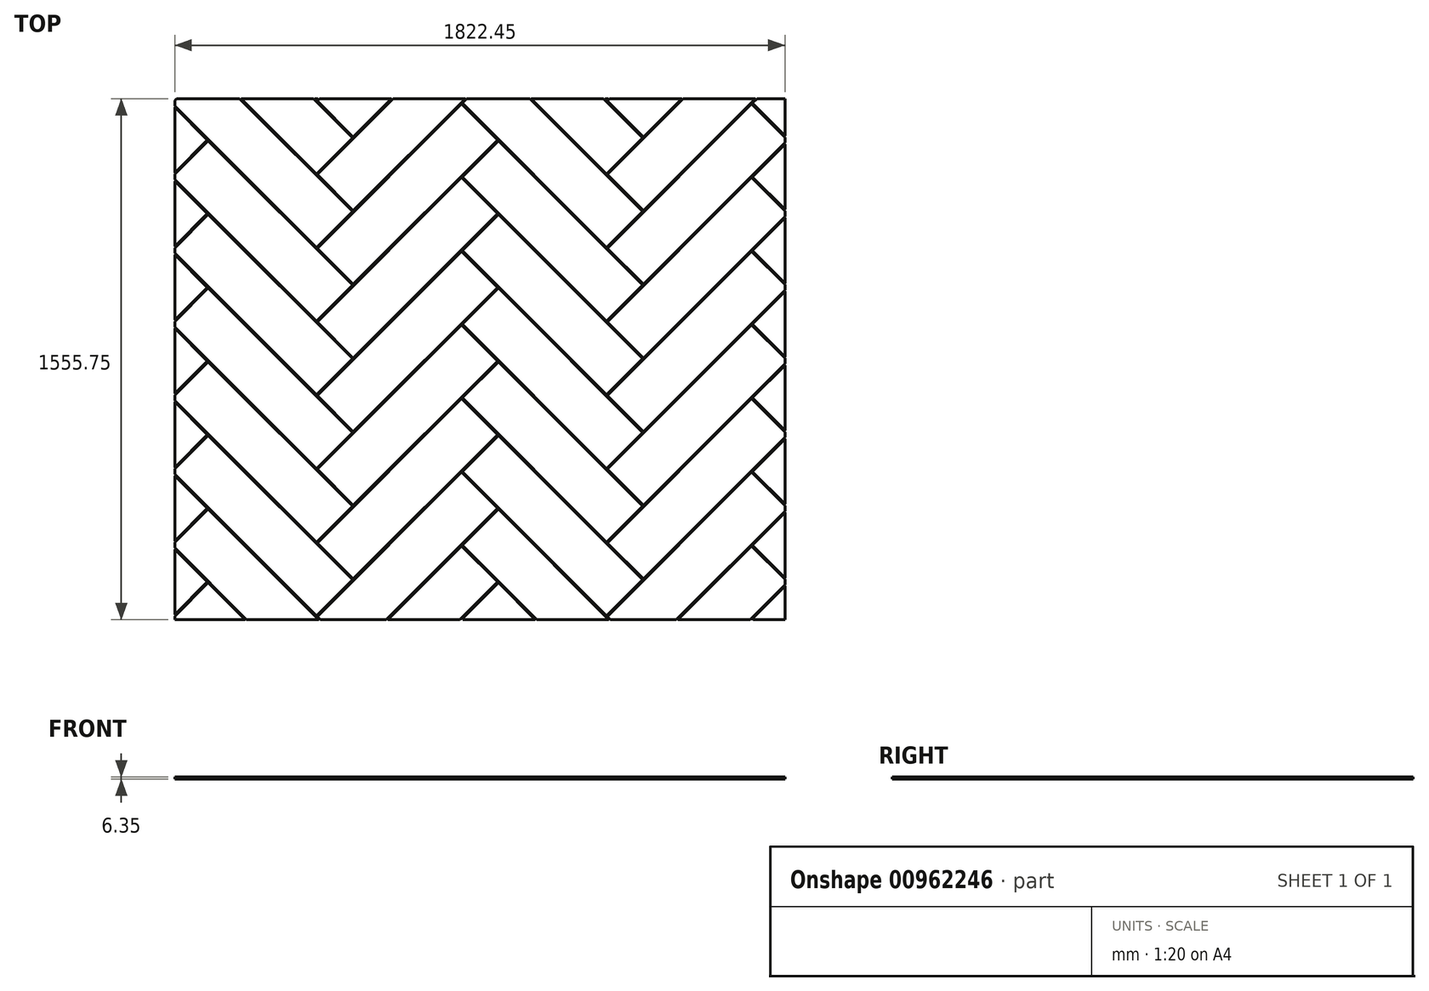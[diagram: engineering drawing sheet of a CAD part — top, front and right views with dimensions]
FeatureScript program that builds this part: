
annotation { "Feature Type Name" : "Feature", "Feature Type Description" : "" }
export const myFeature = defineFeature(function(context is Context, id is Id, definition is map)
    precondition{}
    {
        {
            var Q0;
            Q0=qCreatedBy(makeId("Top.planeOp"),FACE);
            var sketch = newSketch(context, id + "F0", { "sketchPlane" : qUnion([Q0])});
            skLineSegment(sketch, "E0.bottom", {"start": v(0, 0) * mm, "end": v(609.6, 0) * mm});
            skLineSegment(sketch, "E0.top", {"start": v(0, 152.4) * mm, "end": v(609.6, 152.4) * mm});
            skLineSegment(sketch, "E0.left", {"start": v(0, 0) * mm, "end": v(0, 152.4) * mm});
            skLineSegment(sketch, "E0.right", {"start": v(609.6, 0) * mm, "end": v(609.6, 152.4) * mm});
            skLineSegment(sketch, "E1.bottom", {"start": v(152.4, 155.57) * mm, "end": v(152.4, 765.17) * mm});
            skLineSegment(sketch, "E1.top", {"start": v(0, 155.58) * mm, "end": v(0, 765.17) * mm});
            skLineSegment(sketch, "E1.left", {"start": v(152.4, 155.57) * mm, "end": v(0, 155.57) * mm});
            skLineSegment(sketch, "E1.right", {"start": v(152.4, 765.17) * mm, "end": v(0, 765.17) * mm});
            skLineSegment(sketch, "E2.bottom", {"start": v(155.58, 155.57) * mm, "end": v(765.17, 155.57) * mm});
            skLineSegment(sketch, "E2.top", {"start": v(155.58, 307.98) * mm, "end": v(765.17, 307.97) * mm});
            skLineSegment(sketch, "E2.left", {"start": v(155.58, 155.58) * mm, "end": v(155.58, 307.98) * mm});
            skLineSegment(sketch, "E2.right", {"start": v(765.17, 155.57) * mm, "end": v(765.17, 307.97) * mm});
            skLineSegment(sketch, "E3.bottom", {"start": v(307.98, 311.15) * mm, "end": v(307.98, 920.75) * mm});
            skLineSegment(sketch, "E3.top", {"start": v(155.58, 311.15) * mm, "end": v(155.58, 920.75) * mm});
            skLineSegment(sketch, "E3.left", {"start": v(307.98, 311.15) * mm, "end": v(155.58, 311.15) * mm});
            skLineSegment(sketch, "E3.right", {"start": v(307.98, 920.75) * mm, "end": v(155.58, 920.75) * mm});
            skLineSegment(sketch, "E4.0.1.0", {"start": v(-612.78, 612.78) * mm, "end": v(-3.18, 612.78) * mm});
            skLineSegment(sketch, "E4.0.1.1", {"start": v(-460.37, 768.35) * mm, "end": v(-612.77, 768.35) * mm});
            skLineSegment(sketch, "E4.0.1.2", {"start": v(-457.2, 768.35) * mm, "end": v(-457.2, 920.75) * mm});
            skLineSegment(sketch, "E4.0.1.3", {"start": v(-304.8, 923.92) * mm, "end": v(-457.2, 923.92) * mm});
            skLineSegment(sketch, "E4.0.1.4", {"start": v(-457.2, 768.35) * mm, "end": v(152.4, 768.35) * mm});
            skLineSegment(sketch, "E4.0.1.5", {"start": v(-460.37, 768.35) * mm, "end": v(-460.37, 1377.95) * mm});
            skLineSegment(sketch, "E4.0.1.6", {"start": v(-457.2, 920.75) * mm, "end": v(152.4, 920.75) * mm});
            skLineSegment(sketch, "E4.0.1.7", {"start": v(-304.8, 1533.52) * mm, "end": v(-457.2, 1533.52) * mm});
            skLineSegment(sketch, "E4.0.1.8", {"start": v(-612.78, 768.35) * mm, "end": v(-612.77, 1377.95) * mm});
            skLineSegment(sketch, "E4.0.1.9", {"start": v(-457.2, 923.92) * mm, "end": v(-457.2, 1533.52) * mm});
            skLineSegment(sketch, "E4.0.1.10", {"start": v(-3.18, 612.78) * mm, "end": v(-3.18, 765.17) * mm});
            skLineSegment(sketch, "E4.0.1.11", {"start": v(-304.8, 923.92) * mm, "end": v(-304.8, 1533.52) * mm});
            skLineSegment(sketch, "E4.0.1.12", {"start": v(-612.78, 612.78) * mm, "end": v(-612.78, 765.17) * mm});
            skLineSegment(sketch, "E4.0.1.13", {"start": v(-460.37, 1377.95) * mm, "end": v(-612.77, 1377.95) * mm});
            skLineSegment(sketch, "E4.0.1.14", {"start": v(152.4, 768.35) * mm, "end": v(152.4, 920.75) * mm});
            skLineSegment(sketch, "E4.0.1.15", {"start": v(-612.77, 765.17) * mm, "end": v(-3.17, 765.17) * mm});
            skLineSegment(sketch, "E4.1.0.0", {"start": v(311.15, 311.15) * mm, "end": v(920.75, 311.15) * mm});
            skLineSegment(sketch, "E4.1.0.1", {"start": v(463.55, 466.72) * mm, "end": v(311.15, 466.72) * mm});
            skLineSegment(sketch, "E4.1.0.2", {"start": v(466.73, 466.72) * mm, "end": v(466.73, 619.12) * mm});
            skLineSegment(sketch, "E4.1.0.3", {"start": v(619.13, 622.3) * mm, "end": v(466.73, 622.3) * mm});
            skLineSegment(sketch, "E4.1.0.4", {"start": v(466.73, 466.72) * mm, "end": v(1076.33, 466.72) * mm});
            skLineSegment(sketch, "E4.1.0.5", {"start": v(463.55, 466.72) * mm, "end": v(463.55, 1076.32) * mm});
            skLineSegment(sketch, "E4.1.0.6", {"start": v(466.73, 619.12) * mm, "end": v(1076.33, 619.12) * mm});
            skLineSegment(sketch, "E4.1.0.7", {"start": v(619.13, 1231.9) * mm, "end": v(466.73, 1231.9) * mm});
            skLineSegment(sketch, "E4.1.0.8", {"start": v(311.15, 466.72) * mm, "end": v(311.15, 1076.32) * mm});
            skLineSegment(sketch, "E4.1.0.9", {"start": v(466.73, 622.3) * mm, "end": v(466.73, 1231.9) * mm});
            skLineSegment(sketch, "E4.1.0.10", {"start": v(920.75, 311.15) * mm, "end": v(920.75, 463.55) * mm});
            skLineSegment(sketch, "E4.1.0.11", {"start": v(619.13, 622.3) * mm, "end": v(619.13, 1231.9) * mm});
            skLineSegment(sketch, "E4.1.0.12", {"start": v(311.15, 311.15) * mm, "end": v(311.15, 463.55) * mm});
            skLineSegment(sketch, "E4.1.0.13", {"start": v(463.55, 1076.32) * mm, "end": v(311.15, 1076.32) * mm});
            skLineSegment(sketch, "E4.1.0.14", {"start": v(1076.32, 466.72) * mm, "end": v(1076.32, 619.12) * mm});
            skLineSegment(sketch, "E4.1.0.15", {"start": v(311.15, 463.55) * mm, "end": v(920.75, 463.55) * mm});
            skLineSegment(sketch, "E4.1.1.0", {"start": v(-301.62, 923.92) * mm, "end": v(307.98, 923.92) * mm});
            skLineSegment(sketch, "E4.1.1.1", {"start": v(-149.22, 1079.5) * mm, "end": v(-301.62, 1079.5) * mm});
            skLineSegment(sketch, "E4.1.1.2", {"start": v(-146.05, 1079.5) * mm, "end": v(-146.05, 1231.9) * mm});
            skLineSegment(sketch, "E4.1.1.3", {"start": v(6.35, 1235.07) * mm, "end": v(-146.05, 1235.07) * mm});
            skLineSegment(sketch, "E4.1.1.4", {"start": v(-146.05, 1079.5) * mm, "end": v(463.55, 1079.5) * mm});
            skLineSegment(sketch, "E4.1.1.5", {"start": v(-149.22, 1079.5) * mm, "end": v(-149.22, 1689.1) * mm});
            skLineSegment(sketch, "E4.1.1.6", {"start": v(-146.05, 1231.9) * mm, "end": v(463.55, 1231.9) * mm});
            skLineSegment(sketch, "E4.1.1.7", {"start": v(6.35, 1844.67) * mm, "end": v(-146.05, 1844.67) * mm});
            skLineSegment(sketch, "E4.1.1.8", {"start": v(-301.62, 1079.5) * mm, "end": v(-301.62, 1689.1) * mm});
            skLineSegment(sketch, "E4.1.1.9", {"start": v(-146.05, 1235.07) * mm, "end": v(-146.05, 1844.67) * mm});
            skLineSegment(sketch, "E4.1.1.10", {"start": v(307.98, 923.92) * mm, "end": v(307.98, 1076.32) * mm});
            skLineSegment(sketch, "E4.1.1.11", {"start": v(6.35, 1235.07) * mm, "end": v(6.35, 1844.67) * mm});
            skLineSegment(sketch, "E4.1.1.12", {"start": v(-301.62, 923.92) * mm, "end": v(-301.62, 1076.32) * mm});
            skLineSegment(sketch, "E4.1.1.13", {"start": v(-149.22, 1689.1) * mm, "end": v(-301.62, 1689.1) * mm});
            skLineSegment(sketch, "E4.1.1.14", {"start": v(463.55, 1079.5) * mm, "end": v(463.55, 1231.9) * mm});
            skLineSegment(sketch, "E4.1.1.15", {"start": v(-301.62, 1076.32) * mm, "end": v(307.98, 1076.32) * mm});
            skLineSegment(sketch, "E4.2.0.0", {"start": v(622.3, 622.3) * mm, "end": v(1231.9, 622.3) * mm});
            skLineSegment(sketch, "E4.2.0.1", {"start": v(774.7, 777.87) * mm, "end": v(622.3, 777.87) * mm});
            skLineSegment(sketch, "E4.2.0.2", {"start": v(777.88, 777.87) * mm, "end": v(777.88, 930.27) * mm});
            skLineSegment(sketch, "E4.2.0.3", {"start": v(930.28, 933.45) * mm, "end": v(777.88, 933.45) * mm});
            skLineSegment(sketch, "E4.2.0.4", {"start": v(777.88, 777.87) * mm, "end": v(1387.47, 777.87) * mm});
            skLineSegment(sketch, "E4.2.0.5", {"start": v(774.7, 777.87) * mm, "end": v(774.7, 1387.47) * mm});
            skLineSegment(sketch, "E4.2.0.6", {"start": v(777.88, 930.27) * mm, "end": v(1387.47, 930.27) * mm});
            skLineSegment(sketch, "E4.2.0.7", {"start": v(930.28, 1543.05) * mm, "end": v(777.88, 1543.05) * mm});
            skLineSegment(sketch, "E4.2.0.8", {"start": v(622.3, 777.87) * mm, "end": v(622.3, 1387.47) * mm});
            skLineSegment(sketch, "E4.2.0.9", {"start": v(777.88, 933.45) * mm, "end": v(777.88, 1543.05) * mm});
            skLineSegment(sketch, "E4.2.0.10", {"start": v(1231.9, 622.3) * mm, "end": v(1231.9, 774.7) * mm});
            skLineSegment(sketch, "E4.2.0.11", {"start": v(930.28, 933.45) * mm, "end": v(930.28, 1543.05) * mm});
            skLineSegment(sketch, "E4.2.0.12", {"start": v(622.3, 622.3) * mm, "end": v(622.3, 774.7) * mm});
            skLineSegment(sketch, "E4.2.0.13", {"start": v(774.7, 1387.47) * mm, "end": v(622.3, 1387.47) * mm});
            skLineSegment(sketch, "E4.2.0.14", {"start": v(1387.47, 777.87) * mm, "end": v(1387.47, 930.27) * mm});
            skLineSegment(sketch, "E4.2.0.15", {"start": v(622.3, 774.7) * mm, "end": v(1231.9, 774.7) * mm});
            skLineSegment(sketch, "E4.2.1.0", {"start": v(9.53, 1235.07) * mm, "end": v(619.13, 1235.07) * mm});
            skLineSegment(sketch, "E4.2.1.1", {"start": v(161.93, 1390.65) * mm, "end": v(9.53, 1390.65) * mm});
            skLineSegment(sketch, "E4.2.1.2", {"start": v(165.1, 1390.65) * mm, "end": v(165.1, 1543.05) * mm});
            skLineSegment(sketch, "E4.2.1.3", {"start": v(317.5, 1546.22) * mm, "end": v(165.1, 1546.22) * mm});
            skLineSegment(sketch, "E4.2.1.4", {"start": v(165.1, 1390.65) * mm, "end": v(774.7, 1390.65) * mm});
            skLineSegment(sketch, "E4.2.1.5", {"start": v(161.93, 1390.65) * mm, "end": v(161.93, 2000.25) * mm});
            skLineSegment(sketch, "E4.2.1.6", {"start": v(165.1, 1543.05) * mm, "end": v(774.7, 1543.05) * mm});
            skLineSegment(sketch, "E4.2.1.7", {"start": v(317.5, 2155.82) * mm, "end": v(165.1, 2155.82) * mm});
            skLineSegment(sketch, "E4.2.1.8", {"start": v(9.53, 1390.65) * mm, "end": v(9.53, 2000.25) * mm});
            skLineSegment(sketch, "E4.2.1.9", {"start": v(165.1, 1546.22) * mm, "end": v(165.1, 2155.82) * mm});
            skLineSegment(sketch, "E4.2.1.10", {"start": v(619.13, 1235.07) * mm, "end": v(619.13, 1387.47) * mm});
            skLineSegment(sketch, "E4.2.1.11", {"start": v(317.5, 1546.22) * mm, "end": v(317.5, 2155.82) * mm});
            skLineSegment(sketch, "E4.2.1.12", {"start": v(9.53, 1235.07) * mm, "end": v(9.53, 1387.47) * mm});
            skLineSegment(sketch, "E4.2.1.13", {"start": v(161.93, 2000.25) * mm, "end": v(9.53, 2000.25) * mm});
            skLineSegment(sketch, "E4.2.1.14", {"start": v(774.7, 1390.65) * mm, "end": v(774.7, 1543.05) * mm});
            skLineSegment(sketch, "E4.2.1.15", {"start": v(9.53, 1387.47) * mm, "end": v(619.13, 1387.47) * mm});
            skLineSegment(sketch, "E4.direction1", {"start": v(0, 0) * mm, "end": v(311.15, 311.15) * mm, "construction": true});
            skLineSegment(sketch, "E4.direction2", {"start": v(0, 0) * mm, "end": v(-612.78, 612.78) * mm, "construction": true});
            skLineSegment(sketch, "E5.0.3.0", {"start": v(933.45, 933.45) * mm, "end": v(1543.05, 933.45) * mm});
            skLineSegment(sketch, "E5.3.3.0", {"start": v(1085.85, 1089.02) * mm, "end": v(933.45, 1089.02) * mm});
            skLineSegment(sketch, "E5.6.3.0", {"start": v(1089.03, 1089.02) * mm, "end": v(1089.03, 1241.42) * mm});
            skLineSegment(sketch, "E5.9.3.0", {"start": v(1241.43, 1244.6) * mm, "end": v(1089.03, 1244.6) * mm});
            skLineSegment(sketch, "E5.12.3.0", {"start": v(1089.03, 1089.02) * mm, "end": v(1698.62, 1089.02) * mm});
            skLineSegment(sketch, "E5.15.3.0", {"start": v(1085.85, 1089.02) * mm, "end": v(1085.85, 1698.62) * mm});
            skLineSegment(sketch, "E5.18.3.0", {"start": v(1089.03, 1241.42) * mm, "end": v(1698.62, 1241.42) * mm});
            skLineSegment(sketch, "E5.21.3.0", {"start": v(1241.43, 1854.2) * mm, "end": v(1089.03, 1854.2) * mm});
            skLineSegment(sketch, "E5.24.3.0", {"start": v(933.45, 1089.02) * mm, "end": v(933.45, 1698.62) * mm});
            skLineSegment(sketch, "E5.27.3.0", {"start": v(1089.03, 1244.6) * mm, "end": v(1089.03, 1854.2) * mm});
            skLineSegment(sketch, "E5.30.3.0", {"start": v(1543.05, 933.45) * mm, "end": v(1543.05, 1085.85) * mm});
            skLineSegment(sketch, "E5.33.3.0", {"start": v(1241.43, 1244.6) * mm, "end": v(1241.43, 1854.2) * mm});
            skLineSegment(sketch, "E5.36.3.0", {"start": v(933.45, 933.45) * mm, "end": v(933.45, 1085.85) * mm});
            skLineSegment(sketch, "E5.39.3.0", {"start": v(1085.85, 1698.62) * mm, "end": v(933.45, 1698.62) * mm});
            skLineSegment(sketch, "E5.42.3.0", {"start": v(1698.62, 1089.02) * mm, "end": v(1698.62, 1241.42) * mm});
            skLineSegment(sketch, "E5.45.3.0", {"start": v(933.45, 1085.85) * mm, "end": v(1543.05, 1085.85) * mm});
            skLineSegment(sketch, "E5.0.3.1", {"start": v(320.68, 1546.22) * mm, "end": v(930.28, 1546.22) * mm});
            skLineSegment(sketch, "E5.3.3.1", {"start": v(473.08, 1701.8) * mm, "end": v(320.68, 1701.8) * mm});
            skLineSegment(sketch, "E5.6.3.1", {"start": v(476.25, 1701.8) * mm, "end": v(476.25, 1854.2) * mm});
            skLineSegment(sketch, "E5.9.3.1", {"start": v(628.65, 1857.37) * mm, "end": v(476.25, 1857.37) * mm});
            skLineSegment(sketch, "E5.12.3.1", {"start": v(476.25, 1701.8) * mm, "end": v(1085.85, 1701.8) * mm});
            skLineSegment(sketch, "E5.15.3.1", {"start": v(473.08, 1701.8) * mm, "end": v(473.08, 2311.4) * mm});
            skLineSegment(sketch, "E5.18.3.1", {"start": v(476.25, 1854.2) * mm, "end": v(1085.85, 1854.2) * mm});
            skLineSegment(sketch, "E5.21.3.1", {"start": v(628.65, 2466.97) * mm, "end": v(476.25, 2466.97) * mm});
            skLineSegment(sketch, "E5.24.3.1", {"start": v(320.68, 1701.8) * mm, "end": v(320.68, 2311.4) * mm});
            skLineSegment(sketch, "E5.27.3.1", {"start": v(476.25, 1857.37) * mm, "end": v(476.25, 2466.97) * mm});
            skLineSegment(sketch, "E5.30.3.1", {"start": v(930.28, 1546.22) * mm, "end": v(930.28, 1698.62) * mm});
            skLineSegment(sketch, "E5.33.3.1", {"start": v(628.65, 1857.37) * mm, "end": v(628.65, 2466.97) * mm});
            skLineSegment(sketch, "E5.36.3.1", {"start": v(320.68, 1546.22) * mm, "end": v(320.68, 1698.62) * mm});
            skLineSegment(sketch, "E5.39.3.1", {"start": v(473.08, 2311.4) * mm, "end": v(320.68, 2311.4) * mm});
            skLineSegment(sketch, "E5.42.3.1", {"start": v(1085.85, 1701.8) * mm, "end": v(1085.85, 1854.2) * mm});
            skLineSegment(sketch, "E5.45.3.1", {"start": v(320.68, 1698.62) * mm, "end": v(930.28, 1698.62) * mm});
            skLineSegment(sketch, "E5.0.4.0", {"start": v(1244.6, 1244.6) * mm, "end": v(1854.2, 1244.6) * mm});
            skLineSegment(sketch, "E5.3.4.0", {"start": v(1397, 1400.17) * mm, "end": v(1244.6, 1400.17) * mm});
            skLineSegment(sketch, "E5.6.4.0", {"start": v(1400.18, 1400.17) * mm, "end": v(1400.18, 1552.57) * mm});
            skLineSegment(sketch, "E5.9.4.0", {"start": v(1552.58, 1555.75) * mm, "end": v(1400.18, 1555.75) * mm});
            skLineSegment(sketch, "E5.12.4.0", {"start": v(1400.18, 1400.17) * mm, "end": v(2009.78, 1400.17) * mm});
            skLineSegment(sketch, "E5.15.4.0", {"start": v(1397, 1400.17) * mm, "end": v(1397, 2009.77) * mm});
            skLineSegment(sketch, "E5.18.4.0", {"start": v(1400.18, 1552.57) * mm, "end": v(2009.78, 1552.57) * mm});
            skLineSegment(sketch, "E5.21.4.0", {"start": v(1552.58, 2165.35) * mm, "end": v(1400.18, 2165.35) * mm});
            skLineSegment(sketch, "E5.24.4.0", {"start": v(1244.6, 1400.17) * mm, "end": v(1244.6, 2009.77) * mm});
            skLineSegment(sketch, "E5.27.4.0", {"start": v(1400.18, 1555.75) * mm, "end": v(1400.18, 2165.35) * mm});
            skLineSegment(sketch, "E5.30.4.0", {"start": v(1854.2, 1244.6) * mm, "end": v(1854.2, 1397) * mm});
            skLineSegment(sketch, "E5.33.4.0", {"start": v(1552.58, 1555.75) * mm, "end": v(1552.58, 2165.35) * mm});
            skLineSegment(sketch, "E5.36.4.0", {"start": v(1244.6, 1244.6) * mm, "end": v(1244.6, 1397) * mm});
            skLineSegment(sketch, "E5.39.4.0", {"start": v(1397, 2009.77) * mm, "end": v(1244.6, 2009.77) * mm});
            skLineSegment(sketch, "E5.42.4.0", {"start": v(2009.78, 1400.17) * mm, "end": v(2009.78, 1552.57) * mm});
            skLineSegment(sketch, "E5.45.4.0", {"start": v(1244.6, 1397) * mm, "end": v(1854.2, 1397) * mm});
            skLineSegment(sketch, "E5.0.4.1", {"start": v(631.83, 1857.37) * mm, "end": v(1241.43, 1857.37) * mm});
            skLineSegment(sketch, "E5.3.4.1", {"start": v(784.23, 2012.95) * mm, "end": v(631.83, 2012.95) * mm});
            skLineSegment(sketch, "E5.6.4.1", {"start": v(787.4, 2012.95) * mm, "end": v(787.4, 2165.35) * mm});
            skLineSegment(sketch, "E5.9.4.1", {"start": v(939.8, 2168.52) * mm, "end": v(787.4, 2168.52) * mm});
            skLineSegment(sketch, "E5.12.4.1", {"start": v(787.4, 2012.95) * mm, "end": v(1397, 2012.95) * mm});
            skLineSegment(sketch, "E5.15.4.1", {"start": v(784.23, 2012.95) * mm, "end": v(784.23, 2622.55) * mm});
            skLineSegment(sketch, "E5.18.4.1", {"start": v(787.4, 2165.35) * mm, "end": v(1397, 2165.35) * mm});
            skLineSegment(sketch, "E5.21.4.1", {"start": v(939.8, 2778.12) * mm, "end": v(787.4, 2778.12) * mm});
            skLineSegment(sketch, "E5.24.4.1", {"start": v(631.83, 2012.95) * mm, "end": v(631.83, 2622.55) * mm});
            skLineSegment(sketch, "E5.27.4.1", {"start": v(787.4, 2168.52) * mm, "end": v(787.4, 2778.12) * mm});
            skLineSegment(sketch, "E5.30.4.1", {"start": v(1241.43, 1857.37) * mm, "end": v(1241.43, 2009.77) * mm});
            skLineSegment(sketch, "E5.33.4.1", {"start": v(939.8, 2168.52) * mm, "end": v(939.8, 2778.12) * mm});
            skLineSegment(sketch, "E5.36.4.1", {"start": v(631.83, 1857.37) * mm, "end": v(631.83, 2009.77) * mm});
            skLineSegment(sketch, "E5.39.4.1", {"start": v(784.23, 2622.55) * mm, "end": v(631.83, 2622.55) * mm});
            skLineSegment(sketch, "E5.42.4.1", {"start": v(1397, 2012.95) * mm, "end": v(1397, 2165.35) * mm});
            skLineSegment(sketch, "E5.45.4.1", {"start": v(631.83, 2009.77) * mm, "end": v(1241.43, 2009.77) * mm});
            skLineSegment(sketch, "E5.0.5.0", {"start": v(1555.75, 1555.75) * mm, "end": v(2165.35, 1555.75) * mm});
            skLineSegment(sketch, "E5.3.5.0", {"start": v(1708.15, 1711.32) * mm, "end": v(1555.75, 1711.32) * mm});
            skLineSegment(sketch, "E5.6.5.0", {"start": v(1711.33, 1711.32) * mm, "end": v(1711.33, 1863.72) * mm});
            skLineSegment(sketch, "E5.9.5.0", {"start": v(1863.73, 1866.9) * mm, "end": v(1711.33, 1866.9) * mm});
            skLineSegment(sketch, "E5.12.5.0", {"start": v(1711.33, 1711.32) * mm, "end": v(2320.92, 1711.32) * mm});
            skLineSegment(sketch, "E5.15.5.0", {"start": v(1708.15, 1711.32) * mm, "end": v(1708.15, 2320.92) * mm});
            skLineSegment(sketch, "E5.18.5.0", {"start": v(1711.33, 1863.72) * mm, "end": v(2320.92, 1863.72) * mm});
            skLineSegment(sketch, "E5.21.5.0", {"start": v(1863.73, 2476.5) * mm, "end": v(1711.33, 2476.5) * mm});
            skLineSegment(sketch, "E5.24.5.0", {"start": v(1555.75, 1711.32) * mm, "end": v(1555.75, 2320.92) * mm});
            skLineSegment(sketch, "E5.27.5.0", {"start": v(1711.33, 1866.9) * mm, "end": v(1711.33, 2476.5) * mm});
            skLineSegment(sketch, "E5.30.5.0", {"start": v(2165.35, 1555.75) * mm, "end": v(2165.35, 1708.15) * mm});
            skLineSegment(sketch, "E5.33.5.0", {"start": v(1863.73, 1866.9) * mm, "end": v(1863.73, 2476.5) * mm});
            skLineSegment(sketch, "E5.36.5.0", {"start": v(1555.75, 1555.75) * mm, "end": v(1555.75, 1708.15) * mm});
            skLineSegment(sketch, "E5.39.5.0", {"start": v(1708.15, 2320.92) * mm, "end": v(1555.75, 2320.92) * mm});
            skLineSegment(sketch, "E5.42.5.0", {"start": v(2320.92, 1711.32) * mm, "end": v(2320.92, 1863.72) * mm});
            skLineSegment(sketch, "E5.45.5.0", {"start": v(1555.75, 1708.15) * mm, "end": v(2165.35, 1708.15) * mm});
            skLineSegment(sketch, "E5.0.5.1", {"start": v(942.98, 2168.52) * mm, "end": v(1552.58, 2168.52) * mm});
            skLineSegment(sketch, "E5.3.5.1", {"start": v(1095.38, 2324.1) * mm, "end": v(942.98, 2324.1) * mm});
            skLineSegment(sketch, "E5.6.5.1", {"start": v(1098.55, 2324.1) * mm, "end": v(1098.55, 2476.5) * mm});
            skLineSegment(sketch, "E5.9.5.1", {"start": v(1250.95, 2479.67) * mm, "end": v(1098.55, 2479.67) * mm});
            skLineSegment(sketch, "E5.12.5.1", {"start": v(1098.55, 2324.1) * mm, "end": v(1708.15, 2324.1) * mm});
            skLineSegment(sketch, "E5.15.5.1", {"start": v(1095.38, 2324.1) * mm, "end": v(1095.38, 2933.7) * mm});
            skLineSegment(sketch, "E5.18.5.1", {"start": v(1098.55, 2476.5) * mm, "end": v(1708.15, 2476.5) * mm});
            skLineSegment(sketch, "E5.21.5.1", {"start": v(1250.95, 3089.27) * mm, "end": v(1098.55, 3089.27) * mm});
            skLineSegment(sketch, "E5.24.5.1", {"start": v(942.98, 2324.1) * mm, "end": v(942.98, 2933.7) * mm});
            skLineSegment(sketch, "E5.27.5.1", {"start": v(1098.55, 2479.67) * mm, "end": v(1098.55, 3089.27) * mm});
            skLineSegment(sketch, "E5.30.5.1", {"start": v(1552.58, 2168.52) * mm, "end": v(1552.58, 2320.92) * mm});
            skLineSegment(sketch, "E5.33.5.1", {"start": v(1250.95, 2479.67) * mm, "end": v(1250.95, 3089.27) * mm});
            skLineSegment(sketch, "E5.36.5.1", {"start": v(942.98, 2168.52) * mm, "end": v(942.98, 2320.92) * mm});
            skLineSegment(sketch, "E5.39.5.1", {"start": v(1095.38, 2933.7) * mm, "end": v(942.98, 2933.7) * mm});
            skLineSegment(sketch, "E5.42.5.1", {"start": v(1708.15, 2324.1) * mm, "end": v(1708.15, 2476.5) * mm});
            skLineSegment(sketch, "E5.45.5.1", {"start": v(942.98, 2320.92) * mm, "end": v(1552.58, 2320.92) * mm});
            skLineSegment(sketch, "E6.0.0.2", {"start": v(-1225.55, 1225.55) * mm, "end": v(-615.95, 1225.55) * mm});
            skLineSegment(sketch, "E6.3.0.2", {"start": v(-1073.15, 1381.12) * mm, "end": v(-1225.55, 1381.12) * mm});
            skLineSegment(sketch, "E6.6.0.2", {"start": v(-1069.97, 1381.12) * mm, "end": v(-1069.97, 1533.52) * mm});
            skLineSegment(sketch, "E6.9.0.2", {"start": v(-917.57, 1536.7) * mm, "end": v(-1069.97, 1536.7) * mm});
            skLineSegment(sketch, "E6.12.0.2", {"start": v(-1069.97, 1381.12) * mm, "end": v(-460.37, 1381.12) * mm});
            skLineSegment(sketch, "E6.15.0.2", {"start": v(-1073.15, 1381.12) * mm, "end": v(-1073.15, 1990.72) * mm});
            skLineSegment(sketch, "E6.18.0.2", {"start": v(-1069.97, 1533.52) * mm, "end": v(-460.37, 1533.52) * mm});
            skLineSegment(sketch, "E6.21.0.2", {"start": v(-917.57, 2146.3) * mm, "end": v(-1069.97, 2146.3) * mm});
            skLineSegment(sketch, "E6.24.0.2", {"start": v(-1225.55, 1381.12) * mm, "end": v(-1225.55, 1990.72) * mm});
            skLineSegment(sketch, "E6.27.0.2", {"start": v(-1069.97, 1536.7) * mm, "end": v(-1069.97, 2146.3) * mm});
            skLineSegment(sketch, "E6.30.0.2", {"start": v(-615.95, 1225.55) * mm, "end": v(-615.95, 1377.95) * mm});
            skLineSegment(sketch, "E6.33.0.2", {"start": v(-917.57, 1536.7) * mm, "end": v(-917.57, 2146.3) * mm});
            skLineSegment(sketch, "E6.36.0.2", {"start": v(-1225.55, 1225.55) * mm, "end": v(-1225.55, 1377.95) * mm});
            skLineSegment(sketch, "E6.39.0.2", {"start": v(-1073.15, 1990.72) * mm, "end": v(-1225.55, 1990.72) * mm});
            skLineSegment(sketch, "E6.42.0.2", {"start": v(-460.37, 1381.12) * mm, "end": v(-460.37, 1533.52) * mm});
            skLineSegment(sketch, "E6.45.0.2", {"start": v(-1225.55, 1377.95) * mm, "end": v(-615.95, 1377.95) * mm});
            skLineSegment(sketch, "E6.0.0.3", {"start": v(-1838.33, 1838.33) * mm, "end": v(-1228.73, 1838.33) * mm});
            skLineSegment(sketch, "E6.3.0.3", {"start": v(-1685.92, 1993.9) * mm, "end": v(-1838.32, 1993.9) * mm});
            skLineSegment(sketch, "E6.6.0.3", {"start": v(-1682.75, 1993.9) * mm, "end": v(-1682.75, 2146.3) * mm});
            skLineSegment(sketch, "E6.9.0.3", {"start": v(-1530.35, 2149.47) * mm, "end": v(-1682.75, 2149.47) * mm});
            skLineSegment(sketch, "E6.12.0.3", {"start": v(-1682.75, 1993.9) * mm, "end": v(-1073.15, 1993.9) * mm});
            skLineSegment(sketch, "E6.15.0.3", {"start": v(-1685.92, 1993.9) * mm, "end": v(-1685.92, 2603.5) * mm});
            skLineSegment(sketch, "E6.18.0.3", {"start": v(-1682.75, 2146.3) * mm, "end": v(-1073.15, 2146.3) * mm});
            skLineSegment(sketch, "E6.21.0.3", {"start": v(-1530.35, 2759.07) * mm, "end": v(-1682.75, 2759.07) * mm});
            skLineSegment(sketch, "E6.24.0.3", {"start": v(-1838.33, 1993.9) * mm, "end": v(-1838.33, 2603.5) * mm});
            skLineSegment(sketch, "E6.27.0.3", {"start": v(-1682.75, 2149.47) * mm, "end": v(-1682.75, 2759.07) * mm});
            skLineSegment(sketch, "E6.30.0.3", {"start": v(-1228.73, 1838.33) * mm, "end": v(-1228.73, 1990.72) * mm});
            skLineSegment(sketch, "E6.33.0.3", {"start": v(-1530.35, 2149.47) * mm, "end": v(-1530.35, 2759.07) * mm});
            skLineSegment(sketch, "E6.36.0.3", {"start": v(-1838.33, 1838.33) * mm, "end": v(-1838.33, 1990.72) * mm});
            skLineSegment(sketch, "E6.39.0.3", {"start": v(-1685.92, 2603.5) * mm, "end": v(-1838.32, 2603.5) * mm});
            skLineSegment(sketch, "E6.42.0.3", {"start": v(-1073.15, 1993.9) * mm, "end": v(-1073.15, 2146.3) * mm});
            skLineSegment(sketch, "E6.45.0.3", {"start": v(-1838.32, 1990.72) * mm, "end": v(-1228.72, 1990.72) * mm});
            skLineSegment(sketch, "E6.0.0.4", {"start": v(-2451.1, 2451.1) * mm, "end": v(-1841.5, 2451.1) * mm});
            skLineSegment(sketch, "E6.3.0.4", {"start": v(-2298.7, 2606.67) * mm, "end": v(-2451.1, 2606.67) * mm});
            skLineSegment(sketch, "E6.6.0.4", {"start": v(-2295.52, 2606.67) * mm, "end": v(-2295.52, 2759.07) * mm});
            skLineSegment(sketch, "E6.9.0.4", {"start": v(-2143.12, 2762.25) * mm, "end": v(-2295.52, 2762.25) * mm});
            skLineSegment(sketch, "E6.12.0.4", {"start": v(-2295.52, 2606.67) * mm, "end": v(-1685.92, 2606.67) * mm});
            skLineSegment(sketch, "E6.15.0.4", {"start": v(-2298.7, 2606.67) * mm, "end": v(-2298.7, 3216.27) * mm});
            skLineSegment(sketch, "E6.18.0.4", {"start": v(-2295.52, 2759.07) * mm, "end": v(-1685.92, 2759.07) * mm});
            skLineSegment(sketch, "E6.21.0.4", {"start": v(-2143.12, 3371.85) * mm, "end": v(-2295.52, 3371.85) * mm});
            skLineSegment(sketch, "E6.24.0.4", {"start": v(-2451.1, 2606.67) * mm, "end": v(-2451.1, 3216.27) * mm});
            skLineSegment(sketch, "E6.27.0.4", {"start": v(-2295.52, 2762.25) * mm, "end": v(-2295.52, 3371.85) * mm});
            skLineSegment(sketch, "E6.30.0.4", {"start": v(-1841.5, 2451.1) * mm, "end": v(-1841.5, 2603.5) * mm});
            skLineSegment(sketch, "E6.33.0.4", {"start": v(-2143.12, 2762.25) * mm, "end": v(-2143.12, 3371.85) * mm});
            skLineSegment(sketch, "E6.36.0.4", {"start": v(-2451.1, 2451.1) * mm, "end": v(-2451.1, 2603.5) * mm});
            skLineSegment(sketch, "E6.39.0.4", {"start": v(-2298.7, 3216.27) * mm, "end": v(-2451.1, 3216.27) * mm});
            skLineSegment(sketch, "E6.42.0.4", {"start": v(-1685.92, 2606.67) * mm, "end": v(-1685.92, 2759.07) * mm});
            skLineSegment(sketch, "E6.45.0.4", {"start": v(-2451.1, 2603.5) * mm, "end": v(-1841.5, 2603.5) * mm});
            skLineSegment(sketch, "E6.0.1.2", {"start": v(-914.4, 1536.7) * mm, "end": v(-304.8, 1536.7) * mm});
            skLineSegment(sketch, "E6.3.1.2", {"start": v(-762, 1692.27) * mm, "end": v(-914.4, 1692.27) * mm});
            skLineSegment(sketch, "E6.6.1.2", {"start": v(-758.82, 1692.27) * mm, "end": v(-758.82, 1844.67) * mm});
            skLineSegment(sketch, "E6.9.1.2", {"start": v(-606.42, 1847.85) * mm, "end": v(-758.82, 1847.85) * mm});
            skLineSegment(sketch, "E6.12.1.2", {"start": v(-758.82, 1692.27) * mm, "end": v(-149.22, 1692.27) * mm});
            skLineSegment(sketch, "E6.15.1.2", {"start": v(-762, 1692.27) * mm, "end": v(-762, 2301.87) * mm});
            skLineSegment(sketch, "E6.18.1.2", {"start": v(-758.82, 1844.67) * mm, "end": v(-149.22, 1844.67) * mm});
            skLineSegment(sketch, "E6.21.1.2", {"start": v(-606.42, 2457.45) * mm, "end": v(-758.82, 2457.45) * mm});
            skLineSegment(sketch, "E6.24.1.2", {"start": v(-914.4, 1692.27) * mm, "end": v(-914.4, 2301.87) * mm});
            skLineSegment(sketch, "E6.27.1.2", {"start": v(-758.82, 1847.85) * mm, "end": v(-758.82, 2457.45) * mm});
            skLineSegment(sketch, "E6.30.1.2", {"start": v(-304.8, 1536.7) * mm, "end": v(-304.8, 1689.1) * mm});
            skLineSegment(sketch, "E6.33.1.2", {"start": v(-606.42, 1847.85) * mm, "end": v(-606.42, 2457.45) * mm});
            skLineSegment(sketch, "E6.36.1.2", {"start": v(-914.4, 1536.7) * mm, "end": v(-914.4, 1689.1) * mm});
            skLineSegment(sketch, "E6.39.1.2", {"start": v(-762, 2301.87) * mm, "end": v(-914.4, 2301.87) * mm});
            skLineSegment(sketch, "E6.42.1.2", {"start": v(-149.22, 1692.27) * mm, "end": v(-149.22, 1844.67) * mm});
            skLineSegment(sketch, "E6.45.1.2", {"start": v(-914.4, 1689.1) * mm, "end": v(-304.8, 1689.1) * mm});
            skLineSegment(sketch, "E6.0.1.3", {"start": v(-1527.17, 2149.47) * mm, "end": v(-917.57, 2149.47) * mm});
            skLineSegment(sketch, "E6.3.1.3", {"start": v(-1374.77, 2305.05) * mm, "end": v(-1527.17, 2305.05) * mm});
            skLineSegment(sketch, "E6.6.1.3", {"start": v(-1371.6, 2305.05) * mm, "end": v(-1371.6, 2457.45) * mm});
            skLineSegment(sketch, "E6.9.1.3", {"start": v(-1219.2, 2460.62) * mm, "end": v(-1371.6, 2460.62) * mm});
            skLineSegment(sketch, "E6.12.1.3", {"start": v(-1371.6, 2305.05) * mm, "end": v(-762, 2305.05) * mm});
            skLineSegment(sketch, "E6.15.1.3", {"start": v(-1374.77, 2305.05) * mm, "end": v(-1374.77, 2914.65) * mm});
            skLineSegment(sketch, "E6.18.1.3", {"start": v(-1371.6, 2457.45) * mm, "end": v(-762, 2457.45) * mm});
            skLineSegment(sketch, "E6.21.1.3", {"start": v(-1219.2, 3070.22) * mm, "end": v(-1371.6, 3070.22) * mm});
            skLineSegment(sketch, "E6.24.1.3", {"start": v(-1527.17, 2305.05) * mm, "end": v(-1527.17, 2914.65) * mm});
            skLineSegment(sketch, "E6.27.1.3", {"start": v(-1371.6, 2460.62) * mm, "end": v(-1371.6, 3070.22) * mm});
            skLineSegment(sketch, "E6.30.1.3", {"start": v(-917.57, 2149.47) * mm, "end": v(-917.57, 2301.87) * mm});
            skLineSegment(sketch, "E6.33.1.3", {"start": v(-1219.2, 2460.62) * mm, "end": v(-1219.2, 3070.22) * mm});
            skLineSegment(sketch, "E6.36.1.3", {"start": v(-1527.17, 2149.47) * mm, "end": v(-1527.17, 2301.87) * mm});
            skLineSegment(sketch, "E6.39.1.3", {"start": v(-1374.77, 2914.65) * mm, "end": v(-1527.17, 2914.65) * mm});
            skLineSegment(sketch, "E6.42.1.3", {"start": v(-762, 2305.05) * mm, "end": v(-762, 2457.45) * mm});
            skLineSegment(sketch, "E6.45.1.3", {"start": v(-1527.17, 2301.87) * mm, "end": v(-917.57, 2301.87) * mm});
            skLineSegment(sketch, "E6.0.1.4", {"start": v(-2139.95, 2762.25) * mm, "end": v(-1530.35, 2762.25) * mm});
            skLineSegment(sketch, "E6.3.1.4", {"start": v(-1987.55, 2917.82) * mm, "end": v(-2139.95, 2917.82) * mm});
            skLineSegment(sketch, "E6.6.1.4", {"start": v(-1984.37, 2917.82) * mm, "end": v(-1984.37, 3070.22) * mm});
            skLineSegment(sketch, "E6.9.1.4", {"start": v(-1831.97, 3073.4) * mm, "end": v(-1984.37, 3073.4) * mm});
            skLineSegment(sketch, "E6.12.1.4", {"start": v(-1984.37, 2917.82) * mm, "end": v(-1374.77, 2917.82) * mm});
            skLineSegment(sketch, "E6.15.1.4", {"start": v(-1987.55, 2917.82) * mm, "end": v(-1987.55, 3527.42) * mm});
            skLineSegment(sketch, "E6.18.1.4", {"start": v(-1984.37, 3070.22) * mm, "end": v(-1374.77, 3070.22) * mm});
            skLineSegment(sketch, "E6.21.1.4", {"start": v(-1831.97, 3683) * mm, "end": v(-1984.37, 3683) * mm});
            skLineSegment(sketch, "E6.24.1.4", {"start": v(-2139.95, 2917.82) * mm, "end": v(-2139.95, 3527.42) * mm});
            skLineSegment(sketch, "E6.27.1.4", {"start": v(-1984.37, 3073.4) * mm, "end": v(-1984.37, 3683) * mm});
            skLineSegment(sketch, "E6.30.1.4", {"start": v(-1530.35, 2762.25) * mm, "end": v(-1530.35, 2914.65) * mm});
            skLineSegment(sketch, "E6.33.1.4", {"start": v(-1831.97, 3073.4) * mm, "end": v(-1831.97, 3683) * mm});
            skLineSegment(sketch, "E6.36.1.4", {"start": v(-2139.95, 2762.25) * mm, "end": v(-2139.95, 2914.65) * mm});
            skLineSegment(sketch, "E6.39.1.4", {"start": v(-1987.55, 3527.42) * mm, "end": v(-2139.95, 3527.42) * mm});
            skLineSegment(sketch, "E6.42.1.4", {"start": v(-1374.77, 2917.82) * mm, "end": v(-1374.77, 3070.22) * mm});
            skLineSegment(sketch, "E6.45.1.4", {"start": v(-2139.95, 2914.65) * mm, "end": v(-1530.35, 2914.65) * mm});
            skLineSegment(sketch, "E6.0.2.2", {"start": v(-603.25, 1847.85) * mm, "end": v(6.35, 1847.85) * mm});
            skLineSegment(sketch, "E6.3.2.2", {"start": v(-450.85, 2003.42) * mm, "end": v(-603.25, 2003.42) * mm});
            skLineSegment(sketch, "E6.6.2.2", {"start": v(-447.67, 2003.42) * mm, "end": v(-447.67, 2155.82) * mm});
            skLineSegment(sketch, "E6.9.2.2", {"start": v(-295.27, 2159) * mm, "end": v(-447.67, 2159) * mm});
            skLineSegment(sketch, "E6.12.2.2", {"start": v(-447.67, 2003.42) * mm, "end": v(161.93, 2003.42) * mm});
            skLineSegment(sketch, "E6.15.2.2", {"start": v(-450.85, 2003.42) * mm, "end": v(-450.85, 2613.02) * mm});
            skLineSegment(sketch, "E6.18.2.2", {"start": v(-447.67, 2155.82) * mm, "end": v(161.93, 2155.82) * mm});
            skLineSegment(sketch, "E6.21.2.2", {"start": v(-295.27, 2768.6) * mm, "end": v(-447.67, 2768.6) * mm});
            skLineSegment(sketch, "E6.24.2.2", {"start": v(-603.25, 2003.42) * mm, "end": v(-603.25, 2613.02) * mm});
            skLineSegment(sketch, "E6.27.2.2", {"start": v(-447.67, 2159) * mm, "end": v(-447.67, 2768.6) * mm});
            skLineSegment(sketch, "E6.30.2.2", {"start": v(6.35, 1847.85) * mm, "end": v(6.35, 2000.25) * mm});
            skLineSegment(sketch, "E6.33.2.2", {"start": v(-295.27, 2159) * mm, "end": v(-295.27, 2768.6) * mm});
            skLineSegment(sketch, "E6.36.2.2", {"start": v(-603.25, 1847.85) * mm, "end": v(-603.25, 2000.25) * mm});
            skLineSegment(sketch, "E6.39.2.2", {"start": v(-450.85, 2613.02) * mm, "end": v(-603.25, 2613.02) * mm});
            skLineSegment(sketch, "E6.42.2.2", {"start": v(161.93, 2003.42) * mm, "end": v(161.93, 2155.82) * mm});
            skLineSegment(sketch, "E6.45.2.2", {"start": v(-603.25, 2000.25) * mm, "end": v(6.35, 2000.25) * mm});
            skLineSegment(sketch, "E6.0.2.3", {"start": v(-1216.02, 2460.62) * mm, "end": v(-606.42, 2460.62) * mm});
            skLineSegment(sketch, "E6.3.2.3", {"start": v(-1063.62, 2616.2) * mm, "end": v(-1216.02, 2616.2) * mm});
            skLineSegment(sketch, "E6.6.2.3", {"start": v(-1060.45, 2616.2) * mm, "end": v(-1060.45, 2768.6) * mm});
            skLineSegment(sketch, "E6.9.2.3", {"start": v(-908.05, 2771.77) * mm, "end": v(-1060.45, 2771.77) * mm});
            skLineSegment(sketch, "E6.12.2.3", {"start": v(-1060.45, 2616.2) * mm, "end": v(-450.85, 2616.2) * mm});
            skLineSegment(sketch, "E6.15.2.3", {"start": v(-1063.62, 2616.2) * mm, "end": v(-1063.62, 3225.8) * mm});
            skLineSegment(sketch, "E6.18.2.3", {"start": v(-1060.45, 2768.6) * mm, "end": v(-450.85, 2768.6) * mm});
            skLineSegment(sketch, "E6.21.2.3", {"start": v(-908.05, 3381.37) * mm, "end": v(-1060.45, 3381.37) * mm});
            skLineSegment(sketch, "E6.24.2.3", {"start": v(-1216.02, 2616.2) * mm, "end": v(-1216.02, 3225.8) * mm});
            skLineSegment(sketch, "E6.27.2.3", {"start": v(-1060.45, 2771.77) * mm, "end": v(-1060.45, 3381.37) * mm});
            skLineSegment(sketch, "E6.30.2.3", {"start": v(-606.42, 2460.62) * mm, "end": v(-606.42, 2613.02) * mm});
            skLineSegment(sketch, "E6.33.2.3", {"start": v(-908.05, 2771.77) * mm, "end": v(-908.05, 3381.37) * mm});
            skLineSegment(sketch, "E6.36.2.3", {"start": v(-1216.02, 2460.62) * mm, "end": v(-1216.02, 2613.02) * mm});
            skLineSegment(sketch, "E6.39.2.3", {"start": v(-1063.62, 3225.8) * mm, "end": v(-1216.02, 3225.8) * mm});
            skLineSegment(sketch, "E6.42.2.3", {"start": v(-450.85, 2616.2) * mm, "end": v(-450.85, 2768.6) * mm});
            skLineSegment(sketch, "E6.45.2.3", {"start": v(-1216.02, 2613.02) * mm, "end": v(-606.42, 2613.02) * mm});
            skLineSegment(sketch, "E6.0.2.4", {"start": v(-1828.8, 3073.4) * mm, "end": v(-1219.2, 3073.4) * mm});
            skLineSegment(sketch, "E6.3.2.4", {"start": v(-1676.4, 3228.97) * mm, "end": v(-1828.8, 3228.97) * mm});
            skLineSegment(sketch, "E6.6.2.4", {"start": v(-1673.22, 3228.97) * mm, "end": v(-1673.22, 3381.37) * mm});
            skLineSegment(sketch, "E6.9.2.4", {"start": v(-1520.82, 3384.55) * mm, "end": v(-1673.22, 3384.55) * mm});
            skLineSegment(sketch, "E6.12.2.4", {"start": v(-1673.22, 3228.97) * mm, "end": v(-1063.62, 3228.97) * mm});
            skLineSegment(sketch, "E6.15.2.4", {"start": v(-1676.4, 3228.97) * mm, "end": v(-1676.4, 3838.57) * mm});
            skLineSegment(sketch, "E6.18.2.4", {"start": v(-1673.22, 3381.37) * mm, "end": v(-1063.62, 3381.37) * mm});
            skLineSegment(sketch, "E6.21.2.4", {"start": v(-1520.82, 3994.15) * mm, "end": v(-1673.22, 3994.15) * mm});
            skLineSegment(sketch, "E6.24.2.4", {"start": v(-1828.8, 3228.97) * mm, "end": v(-1828.8, 3838.57) * mm});
            skLineSegment(sketch, "E6.27.2.4", {"start": v(-1673.22, 3384.55) * mm, "end": v(-1673.22, 3994.15) * mm});
            skLineSegment(sketch, "E6.30.2.4", {"start": v(-1219.2, 3073.4) * mm, "end": v(-1219.2, 3225.8) * mm});
            skLineSegment(sketch, "E6.33.2.4", {"start": v(-1520.82, 3384.55) * mm, "end": v(-1520.82, 3994.15) * mm});
            skLineSegment(sketch, "E6.36.2.4", {"start": v(-1828.8, 3073.4) * mm, "end": v(-1828.8, 3225.8) * mm});
            skLineSegment(sketch, "E6.39.2.4", {"start": v(-1676.4, 3838.57) * mm, "end": v(-1828.8, 3838.57) * mm});
            skLineSegment(sketch, "E6.42.2.4", {"start": v(-1063.62, 3228.97) * mm, "end": v(-1063.62, 3381.37) * mm});
            skLineSegment(sketch, "E6.45.2.4", {"start": v(-1828.8, 3225.8) * mm, "end": v(-1219.2, 3225.8) * mm});
            skLineSegment(sketch, "E6.0.3.2", {"start": v(-292.1, 2159) * mm, "end": v(317.5, 2159) * mm});
            skLineSegment(sketch, "E6.3.3.2", {"start": v(-139.7, 2314.57) * mm, "end": v(-292.1, 2314.57) * mm});
            skLineSegment(sketch, "E6.6.3.2", {"start": v(-136.52, 2314.57) * mm, "end": v(-136.52, 2466.97) * mm});
            skLineSegment(sketch, "E6.9.3.2", {"start": v(15.88, 2470.15) * mm, "end": v(-136.52, 2470.15) * mm});
            skLineSegment(sketch, "E6.12.3.2", {"start": v(-136.52, 2314.57) * mm, "end": v(473.08, 2314.57) * mm});
            skLineSegment(sketch, "E6.15.3.2", {"start": v(-139.7, 2314.57) * mm, "end": v(-139.7, 2924.17) * mm});
            skLineSegment(sketch, "E6.18.3.2", {"start": v(-136.52, 2466.97) * mm, "end": v(473.08, 2466.97) * mm});
            skLineSegment(sketch, "E6.21.3.2", {"start": v(15.88, 3079.75) * mm, "end": v(-136.52, 3079.75) * mm});
            skLineSegment(sketch, "E6.24.3.2", {"start": v(-292.1, 2314.57) * mm, "end": v(-292.1, 2924.17) * mm});
            skLineSegment(sketch, "E6.27.3.2", {"start": v(-136.52, 2470.15) * mm, "end": v(-136.52, 3079.75) * mm});
            skLineSegment(sketch, "E6.30.3.2", {"start": v(317.5, 2159) * mm, "end": v(317.5, 2311.4) * mm});
            skLineSegment(sketch, "E6.33.3.2", {"start": v(15.88, 2470.15) * mm, "end": v(15.88, 3079.75) * mm});
            skLineSegment(sketch, "E6.36.3.2", {"start": v(-292.1, 2159) * mm, "end": v(-292.1, 2311.4) * mm});
            skLineSegment(sketch, "E6.39.3.2", {"start": v(-139.7, 2924.17) * mm, "end": v(-292.1, 2924.17) * mm});
            skLineSegment(sketch, "E6.42.3.2", {"start": v(473.08, 2314.57) * mm, "end": v(473.08, 2466.97) * mm});
            skLineSegment(sketch, "E6.45.3.2", {"start": v(-292.1, 2311.4) * mm, "end": v(317.5, 2311.4) * mm});
            skLineSegment(sketch, "E6.0.3.3", {"start": v(-904.87, 2771.77) * mm, "end": v(-295.27, 2771.77) * mm});
            skLineSegment(sketch, "E6.3.3.3", {"start": v(-752.47, 2927.35) * mm, "end": v(-904.87, 2927.35) * mm});
            skLineSegment(sketch, "E6.6.3.3", {"start": v(-749.3, 2927.35) * mm, "end": v(-749.3, 3079.75) * mm});
            skLineSegment(sketch, "E6.9.3.3", {"start": v(-596.9, 3082.92) * mm, "end": v(-749.3, 3082.92) * mm});
            skLineSegment(sketch, "E6.12.3.3", {"start": v(-749.3, 2927.35) * mm, "end": v(-139.7, 2927.35) * mm});
            skLineSegment(sketch, "E6.15.3.3", {"start": v(-752.47, 2927.35) * mm, "end": v(-752.47, 3536.95) * mm});
            skLineSegment(sketch, "E6.18.3.3", {"start": v(-749.3, 3079.75) * mm, "end": v(-139.7, 3079.75) * mm});
            skLineSegment(sketch, "E6.21.3.3", {"start": v(-596.9, 3692.52) * mm, "end": v(-749.3, 3692.52) * mm});
            skLineSegment(sketch, "E6.24.3.3", {"start": v(-904.87, 2927.35) * mm, "end": v(-904.87, 3536.95) * mm});
            skLineSegment(sketch, "E6.27.3.3", {"start": v(-749.3, 3082.92) * mm, "end": v(-749.3, 3692.52) * mm});
            skLineSegment(sketch, "E6.30.3.3", {"start": v(-295.27, 2771.77) * mm, "end": v(-295.27, 2924.17) * mm});
            skLineSegment(sketch, "E6.33.3.3", {"start": v(-596.9, 3082.92) * mm, "end": v(-596.9, 3692.52) * mm});
            skLineSegment(sketch, "E6.36.3.3", {"start": v(-904.87, 2771.77) * mm, "end": v(-904.87, 2924.17) * mm});
            skLineSegment(sketch, "E6.39.3.3", {"start": v(-752.47, 3536.95) * mm, "end": v(-904.87, 3536.95) * mm});
            skLineSegment(sketch, "E6.42.3.3", {"start": v(-139.7, 2927.35) * mm, "end": v(-139.7, 3079.75) * mm});
            skLineSegment(sketch, "E6.45.3.3", {"start": v(-904.87, 2924.17) * mm, "end": v(-295.27, 2924.17) * mm});
            skLineSegment(sketch, "E6.0.3.4", {"start": v(-1517.65, 3384.55) * mm, "end": v(-908.05, 3384.55) * mm});
            skLineSegment(sketch, "E6.3.3.4", {"start": v(-1365.25, 3540.12) * mm, "end": v(-1517.65, 3540.12) * mm});
            skLineSegment(sketch, "E6.6.3.4", {"start": v(-1362.07, 3540.12) * mm, "end": v(-1362.07, 3692.52) * mm});
            skLineSegment(sketch, "E6.9.3.4", {"start": v(-1209.67, 3695.7) * mm, "end": v(-1362.07, 3695.7) * mm});
            skLineSegment(sketch, "E6.12.3.4", {"start": v(-1362.07, 3540.12) * mm, "end": v(-752.47, 3540.12) * mm});
            skLineSegment(sketch, "E6.15.3.4", {"start": v(-1365.25, 3540.12) * mm, "end": v(-1365.25, 4149.72) * mm});
            skLineSegment(sketch, "E6.18.3.4", {"start": v(-1362.07, 3692.52) * mm, "end": v(-752.47, 3692.52) * mm});
            skLineSegment(sketch, "E6.21.3.4", {"start": v(-1209.67, 4305.3) * mm, "end": v(-1362.07, 4305.3) * mm});
            skLineSegment(sketch, "E6.24.3.4", {"start": v(-1517.65, 3540.12) * mm, "end": v(-1517.65, 4149.72) * mm});
            skLineSegment(sketch, "E6.27.3.4", {"start": v(-1362.07, 3695.7) * mm, "end": v(-1362.07, 4305.3) * mm});
            skLineSegment(sketch, "E6.30.3.4", {"start": v(-908.05, 3384.55) * mm, "end": v(-908.05, 3536.95) * mm});
            skLineSegment(sketch, "E6.33.3.4", {"start": v(-1209.67, 3695.7) * mm, "end": v(-1209.67, 4305.3) * mm});
            skLineSegment(sketch, "E6.36.3.4", {"start": v(-1517.65, 3384.55) * mm, "end": v(-1517.65, 3536.95) * mm});
            skLineSegment(sketch, "E6.39.3.4", {"start": v(-1365.25, 4149.72) * mm, "end": v(-1517.65, 4149.72) * mm});
            skLineSegment(sketch, "E6.42.3.4", {"start": v(-752.47, 3540.12) * mm, "end": v(-752.47, 3692.52) * mm});
            skLineSegment(sketch, "E6.45.3.4", {"start": v(-1517.65, 3536.95) * mm, "end": v(-908.05, 3536.95) * mm});
            skLineSegment(sketch, "E6.0.4.2", {"start": v(19.05, 2470.15) * mm, "end": v(628.65, 2470.15) * mm});
            skLineSegment(sketch, "E6.3.4.2", {"start": v(171.45, 2625.72) * mm, "end": v(19.05, 2625.72) * mm});
            skLineSegment(sketch, "E6.6.4.2", {"start": v(174.63, 2625.72) * mm, "end": v(174.63, 2778.12) * mm});
            skLineSegment(sketch, "E6.9.4.2", {"start": v(327.03, 2781.3) * mm, "end": v(174.63, 2781.3) * mm});
            skLineSegment(sketch, "E6.12.4.2", {"start": v(174.63, 2625.72) * mm, "end": v(784.23, 2625.72) * mm});
            skLineSegment(sketch, "E6.15.4.2", {"start": v(171.45, 2625.72) * mm, "end": v(171.45, 3235.32) * mm});
            skLineSegment(sketch, "E6.18.4.2", {"start": v(174.63, 2778.12) * mm, "end": v(784.23, 2778.12) * mm});
            skLineSegment(sketch, "E6.21.4.2", {"start": v(327.03, 3390.9) * mm, "end": v(174.63, 3390.9) * mm});
            skLineSegment(sketch, "E6.24.4.2", {"start": v(19.05, 2625.72) * mm, "end": v(19.05, 3235.32) * mm});
            skLineSegment(sketch, "E6.27.4.2", {"start": v(174.63, 2781.3) * mm, "end": v(174.63, 3390.9) * mm});
            skLineSegment(sketch, "E6.30.4.2", {"start": v(628.65, 2470.15) * mm, "end": v(628.65, 2622.55) * mm});
            skLineSegment(sketch, "E6.33.4.2", {"start": v(327.03, 2781.3) * mm, "end": v(327.03, 3390.9) * mm});
            skLineSegment(sketch, "E6.36.4.2", {"start": v(19.05, 2470.15) * mm, "end": v(19.05, 2622.55) * mm});
            skLineSegment(sketch, "E6.39.4.2", {"start": v(171.45, 3235.32) * mm, "end": v(19.05, 3235.32) * mm});
            skLineSegment(sketch, "E6.42.4.2", {"start": v(784.23, 2625.72) * mm, "end": v(784.23, 2778.12) * mm});
            skLineSegment(sketch, "E6.45.4.2", {"start": v(19.05, 2622.55) * mm, "end": v(628.65, 2622.55) * mm});
            skLineSegment(sketch, "E6.0.4.3", {"start": v(-593.72, 3082.92) * mm, "end": v(15.88, 3082.92) * mm});
            skLineSegment(sketch, "E6.3.4.3", {"start": v(-441.32, 3238.5) * mm, "end": v(-593.72, 3238.5) * mm});
            skLineSegment(sketch, "E6.6.4.3", {"start": v(-438.15, 3238.5) * mm, "end": v(-438.15, 3390.9) * mm});
            skLineSegment(sketch, "E6.9.4.3", {"start": v(-285.75, 3394.07) * mm, "end": v(-438.15, 3394.07) * mm});
            skLineSegment(sketch, "E6.12.4.3", {"start": v(-438.15, 3238.5) * mm, "end": v(171.45, 3238.5) * mm});
            skLineSegment(sketch, "E6.15.4.3", {"start": v(-441.32, 3238.5) * mm, "end": v(-441.32, 3848.1) * mm});
            skLineSegment(sketch, "E6.18.4.3", {"start": v(-438.15, 3390.9) * mm, "end": v(171.45, 3390.9) * mm});
            skLineSegment(sketch, "E6.21.4.3", {"start": v(-285.75, 4003.67) * mm, "end": v(-438.15, 4003.67) * mm});
            skLineSegment(sketch, "E6.24.4.3", {"start": v(-593.72, 3238.5) * mm, "end": v(-593.72, 3848.1) * mm});
            skLineSegment(sketch, "E6.27.4.3", {"start": v(-438.15, 3394.07) * mm, "end": v(-438.15, 4003.67) * mm});
            skLineSegment(sketch, "E6.30.4.3", {"start": v(15.88, 3082.92) * mm, "end": v(15.88, 3235.32) * mm});
            skLineSegment(sketch, "E6.33.4.3", {"start": v(-285.75, 3394.07) * mm, "end": v(-285.75, 4003.67) * mm});
            skLineSegment(sketch, "E6.36.4.3", {"start": v(-593.72, 3082.92) * mm, "end": v(-593.72, 3235.32) * mm});
            skLineSegment(sketch, "E6.39.4.3", {"start": v(-441.32, 3848.1) * mm, "end": v(-593.72, 3848.1) * mm});
            skLineSegment(sketch, "E6.42.4.3", {"start": v(171.45, 3238.5) * mm, "end": v(171.45, 3390.9) * mm});
            skLineSegment(sketch, "E6.45.4.3", {"start": v(-593.72, 3235.32) * mm, "end": v(15.88, 3235.32) * mm});
            skLineSegment(sketch, "E6.0.4.4", {"start": v(-1206.5, 3695.7) * mm, "end": v(-596.9, 3695.7) * mm});
            skLineSegment(sketch, "E6.3.4.4", {"start": v(-1054.1, 3851.27) * mm, "end": v(-1206.5, 3851.27) * mm});
            skLineSegment(sketch, "E6.6.4.4", {"start": v(-1050.92, 3851.27) * mm, "end": v(-1050.92, 4003.67) * mm});
            skLineSegment(sketch, "E6.9.4.4", {"start": v(-898.52, 4006.85) * mm, "end": v(-1050.92, 4006.85) * mm});
            skLineSegment(sketch, "E6.12.4.4", {"start": v(-1050.92, 3851.27) * mm, "end": v(-441.32, 3851.27) * mm});
            skLineSegment(sketch, "E6.15.4.4", {"start": v(-1054.1, 3851.27) * mm, "end": v(-1054.1, 4460.87) * mm});
            skLineSegment(sketch, "E6.18.4.4", {"start": v(-1050.92, 4003.67) * mm, "end": v(-441.32, 4003.67) * mm});
            skLineSegment(sketch, "E6.21.4.4", {"start": v(-898.52, 4616.45) * mm, "end": v(-1050.92, 4616.45) * mm});
            skLineSegment(sketch, "E6.24.4.4", {"start": v(-1206.5, 3851.27) * mm, "end": v(-1206.5, 4460.87) * mm});
            skLineSegment(sketch, "E6.27.4.4", {"start": v(-1050.92, 4006.85) * mm, "end": v(-1050.92, 4616.45) * mm});
            skLineSegment(sketch, "E6.30.4.4", {"start": v(-596.9, 3695.7) * mm, "end": v(-596.9, 3848.1) * mm});
            skLineSegment(sketch, "E6.33.4.4", {"start": v(-898.52, 4006.85) * mm, "end": v(-898.52, 4616.45) * mm});
            skLineSegment(sketch, "E6.36.4.4", {"start": v(-1206.5, 3695.7) * mm, "end": v(-1206.5, 3848.1) * mm});
            skLineSegment(sketch, "E6.39.4.4", {"start": v(-1054.1, 4460.87) * mm, "end": v(-1206.5, 4460.87) * mm});
            skLineSegment(sketch, "E6.42.4.4", {"start": v(-441.32, 3851.27) * mm, "end": v(-441.32, 4003.67) * mm});
            skLineSegment(sketch, "E6.45.4.4", {"start": v(-1206.5, 3848.1) * mm, "end": v(-596.9, 3848.1) * mm});
            skLineSegment(sketch, "E6.0.5.2", {"start": v(330.2, 2781.3) * mm, "end": v(939.8, 2781.3) * mm});
            skLineSegment(sketch, "E6.3.5.2", {"start": v(482.6, 2936.87) * mm, "end": v(330.2, 2936.87) * mm});
            skLineSegment(sketch, "E6.6.5.2", {"start": v(485.78, 2936.87) * mm, "end": v(485.78, 3089.27) * mm});
            skLineSegment(sketch, "E6.9.5.2", {"start": v(638.18, 3092.45) * mm, "end": v(485.78, 3092.45) * mm});
            skLineSegment(sketch, "E6.12.5.2", {"start": v(485.78, 2936.87) * mm, "end": v(1095.38, 2936.87) * mm});
            skLineSegment(sketch, "E6.15.5.2", {"start": v(482.6, 2936.87) * mm, "end": v(482.6, 3546.47) * mm});
            skLineSegment(sketch, "E6.18.5.2", {"start": v(485.78, 3089.27) * mm, "end": v(1095.38, 3089.27) * mm});
            skLineSegment(sketch, "E6.21.5.2", {"start": v(638.18, 3702.05) * mm, "end": v(485.78, 3702.05) * mm});
            skLineSegment(sketch, "E6.24.5.2", {"start": v(330.2, 2936.87) * mm, "end": v(330.2, 3546.47) * mm});
            skLineSegment(sketch, "E6.27.5.2", {"start": v(485.78, 3092.45) * mm, "end": v(485.78, 3702.05) * mm});
            skLineSegment(sketch, "E6.30.5.2", {"start": v(939.8, 2781.3) * mm, "end": v(939.8, 2933.7) * mm});
            skLineSegment(sketch, "E6.33.5.2", {"start": v(638.18, 3092.45) * mm, "end": v(638.18, 3702.05) * mm});
            skLineSegment(sketch, "E6.36.5.2", {"start": v(330.2, 2781.3) * mm, "end": v(330.2, 2933.7) * mm});
            skLineSegment(sketch, "E6.39.5.2", {"start": v(482.6, 3546.47) * mm, "end": v(330.2, 3546.47) * mm});
            skLineSegment(sketch, "E6.42.5.2", {"start": v(1095.38, 2936.87) * mm, "end": v(1095.38, 3089.27) * mm});
            skLineSegment(sketch, "E6.45.5.2", {"start": v(330.2, 2933.7) * mm, "end": v(939.8, 2933.7) * mm});
            skLineSegment(sketch, "E6.0.5.3", {"start": v(-282.57, 3394.07) * mm, "end": v(327.03, 3394.07) * mm});
            skLineSegment(sketch, "E6.3.5.3", {"start": v(-130.17, 3549.65) * mm, "end": v(-282.57, 3549.65) * mm});
            skLineSegment(sketch, "E6.6.5.3", {"start": v(-127, 3549.65) * mm, "end": v(-127, 3702.05) * mm});
            skLineSegment(sketch, "E6.9.5.3", {"start": v(25.4, 3705.22) * mm, "end": v(-127, 3705.22) * mm});
            skLineSegment(sketch, "E6.12.5.3", {"start": v(-127, 3549.65) * mm, "end": v(482.6, 3549.65) * mm});
            skLineSegment(sketch, "E6.15.5.3", {"start": v(-130.17, 3549.65) * mm, "end": v(-130.17, 4159.25) * mm});
            skLineSegment(sketch, "E6.18.5.3", {"start": v(-127, 3702.05) * mm, "end": v(482.6, 3702.05) * mm});
            skLineSegment(sketch, "E6.21.5.3", {"start": v(25.4, 4314.82) * mm, "end": v(-127, 4314.82) * mm});
            skLineSegment(sketch, "E6.24.5.3", {"start": v(-282.57, 3549.65) * mm, "end": v(-282.57, 4159.25) * mm});
            skLineSegment(sketch, "E6.27.5.3", {"start": v(-127, 3705.22) * mm, "end": v(-127, 4314.82) * mm});
            skLineSegment(sketch, "E6.30.5.3", {"start": v(327.03, 3394.07) * mm, "end": v(327.03, 3546.47) * mm});
            skLineSegment(sketch, "E6.33.5.3", {"start": v(25.4, 3705.22) * mm, "end": v(25.4, 4314.82) * mm});
            skLineSegment(sketch, "E6.36.5.3", {"start": v(-282.57, 3394.07) * mm, "end": v(-282.57, 3546.47) * mm});
            skLineSegment(sketch, "E6.39.5.3", {"start": v(-130.17, 4159.25) * mm, "end": v(-282.57, 4159.25) * mm});
            skLineSegment(sketch, "E6.42.5.3", {"start": v(482.6, 3549.65) * mm, "end": v(482.6, 3702.05) * mm});
            skLineSegment(sketch, "E6.45.5.3", {"start": v(-282.57, 3546.47) * mm, "end": v(327.03, 3546.47) * mm});
            skLineSegment(sketch, "E6.0.5.4", {"start": v(-895.35, 4006.85) * mm, "end": v(-285.75, 4006.85) * mm});
            skLineSegment(sketch, "E6.3.5.4", {"start": v(-742.95, 4162.42) * mm, "end": v(-895.35, 4162.42) * mm});
            skLineSegment(sketch, "E6.6.5.4", {"start": v(-739.77, 4162.42) * mm, "end": v(-739.77, 4314.82) * mm});
            skLineSegment(sketch, "E6.9.5.4", {"start": v(-587.37, 4318) * mm, "end": v(-739.77, 4318) * mm});
            skLineSegment(sketch, "E6.12.5.4", {"start": v(-739.77, 4162.42) * mm, "end": v(-130.17, 4162.42) * mm});
            skLineSegment(sketch, "E6.15.5.4", {"start": v(-742.95, 4162.42) * mm, "end": v(-742.95, 4772.02) * mm});
            skLineSegment(sketch, "E6.18.5.4", {"start": v(-739.77, 4314.82) * mm, "end": v(-130.17, 4314.82) * mm});
            skLineSegment(sketch, "E6.21.5.4", {"start": v(-587.37, 4927.6) * mm, "end": v(-739.77, 4927.6) * mm});
            skLineSegment(sketch, "E6.24.5.4", {"start": v(-895.35, 4162.42) * mm, "end": v(-895.35, 4772.02) * mm});
            skLineSegment(sketch, "E6.27.5.4", {"start": v(-739.77, 4318) * mm, "end": v(-739.77, 4927.6) * mm});
            skLineSegment(sketch, "E6.30.5.4", {"start": v(-285.75, 4006.85) * mm, "end": v(-285.75, 4159.25) * mm});
            skLineSegment(sketch, "E6.33.5.4", {"start": v(-587.37, 4318) * mm, "end": v(-587.37, 4927.6) * mm});
            skLineSegment(sketch, "E6.36.5.4", {"start": v(-895.35, 4006.85) * mm, "end": v(-895.35, 4159.25) * mm});
            skLineSegment(sketch, "E6.39.5.4", {"start": v(-742.95, 4772.02) * mm, "end": v(-895.35, 4772.02) * mm});
            skLineSegment(sketch, "E6.42.5.4", {"start": v(-130.17, 4162.42) * mm, "end": v(-130.17, 4314.82) * mm});
            skLineSegment(sketch, "E6.45.5.4", {"start": v(-895.35, 4159.25) * mm, "end": v(-285.75, 4159.25) * mm});
            skLineSegment(sketch, "E7.0.6.0", {"start": v(1866.9, 1866.9) * mm, "end": v(2476.5, 1866.9) * mm});
            skLineSegment(sketch, "E7.3.6.0", {"start": v(2019.3, 2022.47) * mm, "end": v(1866.9, 2022.47) * mm});
            skLineSegment(sketch, "E7.6.6.0", {"start": v(2022.48, 2022.47) * mm, "end": v(2022.48, 2174.87) * mm});
            skLineSegment(sketch, "E7.9.6.0", {"start": v(2174.88, 2178.05) * mm, "end": v(2022.48, 2178.05) * mm});
            skLineSegment(sketch, "E7.12.6.0", {"start": v(2022.48, 2022.47) * mm, "end": v(2632.08, 2022.47) * mm});
            skLineSegment(sketch, "E7.15.6.0", {"start": v(2019.3, 2022.47) * mm, "end": v(2019.3, 2632.07) * mm});
            skLineSegment(sketch, "E7.18.6.0", {"start": v(2022.48, 2174.87) * mm, "end": v(2632.08, 2174.87) * mm});
            skLineSegment(sketch, "E7.21.6.0", {"start": v(2174.88, 2787.65) * mm, "end": v(2022.48, 2787.65) * mm});
            skLineSegment(sketch, "E7.24.6.0", {"start": v(1866.9, 2022.47) * mm, "end": v(1866.9, 2632.07) * mm});
            skLineSegment(sketch, "E7.27.6.0", {"start": v(2022.48, 2178.05) * mm, "end": v(2022.48, 2787.65) * mm});
            skLineSegment(sketch, "E7.30.6.0", {"start": v(2476.5, 1866.9) * mm, "end": v(2476.5, 2019.3) * mm});
            skLineSegment(sketch, "E7.33.6.0", {"start": v(2174.88, 2178.05) * mm, "end": v(2174.88, 2787.65) * mm});
            skLineSegment(sketch, "E7.36.6.0", {"start": v(1866.9, 1866.9) * mm, "end": v(1866.9, 2019.3) * mm});
            skLineSegment(sketch, "E7.39.6.0", {"start": v(2019.3, 2632.07) * mm, "end": v(1866.9, 2632.07) * mm});
            skLineSegment(sketch, "E7.42.6.0", {"start": v(2632.08, 2022.47) * mm, "end": v(2632.08, 2174.87) * mm});
            skLineSegment(sketch, "E7.45.6.0", {"start": v(1866.9, 2019.3) * mm, "end": v(2476.5, 2019.3) * mm});
            skLineSegment(sketch, "E7.0.6.1", {"start": v(1254.13, 2479.67) * mm, "end": v(1863.73, 2479.67) * mm});
            skLineSegment(sketch, "E7.3.6.1", {"start": v(1406.53, 2635.25) * mm, "end": v(1254.13, 2635.25) * mm});
            skLineSegment(sketch, "E7.6.6.1", {"start": v(1409.7, 2635.25) * mm, "end": v(1409.7, 2787.65) * mm});
            skLineSegment(sketch, "E7.9.6.1", {"start": v(1562.1, 2790.82) * mm, "end": v(1409.7, 2790.82) * mm});
            skLineSegment(sketch, "E7.12.6.1", {"start": v(1409.7, 2635.25) * mm, "end": v(2019.3, 2635.25) * mm});
            skLineSegment(sketch, "E7.15.6.1", {"start": v(1406.53, 2635.25) * mm, "end": v(1406.53, 3244.85) * mm});
            skLineSegment(sketch, "E7.18.6.1", {"start": v(1409.7, 2787.65) * mm, "end": v(2019.3, 2787.65) * mm});
            skLineSegment(sketch, "E7.21.6.1", {"start": v(1562.1, 3400.42) * mm, "end": v(1409.7, 3400.42) * mm});
            skLineSegment(sketch, "E7.24.6.1", {"start": v(1254.13, 2635.25) * mm, "end": v(1254.13, 3244.85) * mm});
            skLineSegment(sketch, "E7.27.6.1", {"start": v(1409.7, 2790.82) * mm, "end": v(1409.7, 3400.42) * mm});
            skLineSegment(sketch, "E7.30.6.1", {"start": v(1863.73, 2479.67) * mm, "end": v(1863.73, 2632.07) * mm});
            skLineSegment(sketch, "E7.33.6.1", {"start": v(1562.1, 2790.82) * mm, "end": v(1562.1, 3400.42) * mm});
            skLineSegment(sketch, "E7.36.6.1", {"start": v(1254.13, 2479.67) * mm, "end": v(1254.13, 2632.07) * mm});
            skLineSegment(sketch, "E7.39.6.1", {"start": v(1406.53, 3244.85) * mm, "end": v(1254.13, 3244.85) * mm});
            skLineSegment(sketch, "E7.42.6.1", {"start": v(2019.3, 2635.25) * mm, "end": v(2019.3, 2787.65) * mm});
            skLineSegment(sketch, "E7.45.6.1", {"start": v(1254.13, 2632.07) * mm, "end": v(1863.73, 2632.07) * mm});
            skLineSegment(sketch, "E7.0.6.2", {"start": v(641.35, 3092.45) * mm, "end": v(1250.95, 3092.45) * mm});
            skLineSegment(sketch, "E7.3.6.2", {"start": v(793.75, 3248.02) * mm, "end": v(641.35, 3248.02) * mm});
            skLineSegment(sketch, "E7.6.6.2", {"start": v(796.92, 3248.02) * mm, "end": v(796.92, 3400.42) * mm});
            skLineSegment(sketch, "E7.9.6.2", {"start": v(949.32, 3403.6) * mm, "end": v(796.92, 3403.6) * mm});
            skLineSegment(sketch, "E7.12.6.2", {"start": v(796.92, 3248.02) * mm, "end": v(1406.52, 3248.02) * mm});
            skLineSegment(sketch, "E7.15.6.2", {"start": v(793.75, 3248.02) * mm, "end": v(793.75, 3857.62) * mm});
            skLineSegment(sketch, "E7.18.6.2", {"start": v(796.92, 3400.42) * mm, "end": v(1406.52, 3400.42) * mm});
            skLineSegment(sketch, "E7.21.6.2", {"start": v(949.32, 4013.2) * mm, "end": v(796.92, 4013.2) * mm});
            skLineSegment(sketch, "E7.24.6.2", {"start": v(641.35, 3248.02) * mm, "end": v(641.35, 3857.62) * mm});
            skLineSegment(sketch, "E7.27.6.2", {"start": v(796.92, 3403.6) * mm, "end": v(796.92, 4013.2) * mm});
            skLineSegment(sketch, "E7.30.6.2", {"start": v(1250.95, 3092.45) * mm, "end": v(1250.95, 3244.85) * mm});
            skLineSegment(sketch, "E7.33.6.2", {"start": v(949.32, 3403.6) * mm, "end": v(949.32, 4013.2) * mm});
            skLineSegment(sketch, "E7.36.6.2", {"start": v(641.35, 3092.45) * mm, "end": v(641.35, 3244.85) * mm});
            skLineSegment(sketch, "E7.39.6.2", {"start": v(793.75, 3857.62) * mm, "end": v(641.35, 3857.62) * mm});
            skLineSegment(sketch, "E7.42.6.2", {"start": v(1406.52, 3248.02) * mm, "end": v(1406.52, 3400.42) * mm});
            skLineSegment(sketch, "E7.45.6.2", {"start": v(641.35, 3244.85) * mm, "end": v(1250.95, 3244.85) * mm});
            skLineSegment(sketch, "E7.0.6.3", {"start": v(28.57, 3705.22) * mm, "end": v(638.17, 3705.22) * mm});
            skLineSegment(sketch, "E7.3.6.3", {"start": v(180.97, 3860.8) * mm, "end": v(28.57, 3860.8) * mm});
            skLineSegment(sketch, "E7.6.6.3", {"start": v(184.15, 3860.8) * mm, "end": v(184.15, 4013.2) * mm});
            skLineSegment(sketch, "E7.9.6.3", {"start": v(336.55, 4016.37) * mm, "end": v(184.15, 4016.37) * mm});
            skLineSegment(sketch, "E7.12.6.3", {"start": v(184.15, 3860.8) * mm, "end": v(793.75, 3860.8) * mm});
            skLineSegment(sketch, "E7.15.6.3", {"start": v(180.97, 3860.8) * mm, "end": v(180.97, 4470.4) * mm});
            skLineSegment(sketch, "E7.18.6.3", {"start": v(184.15, 4013.2) * mm, "end": v(793.75, 4013.2) * mm});
            skLineSegment(sketch, "E7.21.6.3", {"start": v(336.55, 4625.97) * mm, "end": v(184.15, 4625.97) * mm});
            skLineSegment(sketch, "E7.24.6.3", {"start": v(28.57, 3860.8) * mm, "end": v(28.57, 4470.4) * mm});
            skLineSegment(sketch, "E7.27.6.3", {"start": v(184.15, 4016.37) * mm, "end": v(184.15, 4625.97) * mm});
            skLineSegment(sketch, "E7.30.6.3", {"start": v(638.17, 3705.22) * mm, "end": v(638.17, 3857.62) * mm});
            skLineSegment(sketch, "E7.33.6.3", {"start": v(336.55, 4016.37) * mm, "end": v(336.55, 4625.97) * mm});
            skLineSegment(sketch, "E7.36.6.3", {"start": v(28.57, 3705.22) * mm, "end": v(28.57, 3857.62) * mm});
            skLineSegment(sketch, "E7.39.6.3", {"start": v(180.97, 4470.4) * mm, "end": v(28.57, 4470.4) * mm});
            skLineSegment(sketch, "E7.42.6.3", {"start": v(793.75, 3860.8) * mm, "end": v(793.75, 4013.2) * mm});
            skLineSegment(sketch, "E7.45.6.3", {"start": v(28.57, 3857.62) * mm, "end": v(638.17, 3857.62) * mm});
            skLineSegment(sketch, "E7.0.6.4", {"start": v(-584.2, 4318) * mm, "end": v(25.4, 4318) * mm});
            skLineSegment(sketch, "E7.3.6.4", {"start": v(-431.8, 4473.57) * mm, "end": v(-584.2, 4473.57) * mm});
            skLineSegment(sketch, "E7.6.6.4", {"start": v(-428.63, 4473.57) * mm, "end": v(-428.63, 4625.97) * mm});
            skLineSegment(sketch, "E7.9.6.4", {"start": v(-276.23, 4629.15) * mm, "end": v(-428.63, 4629.15) * mm});
            skLineSegment(sketch, "E7.12.6.4", {"start": v(-428.63, 4473.57) * mm, "end": v(180.97, 4473.57) * mm});
            skLineSegment(sketch, "E7.15.6.4", {"start": v(-431.8, 4473.57) * mm, "end": v(-431.8, 5083.18) * mm});
            skLineSegment(sketch, "E7.18.6.4", {"start": v(-428.63, 4625.97) * mm, "end": v(180.97, 4625.97) * mm});
            skLineSegment(sketch, "E7.21.6.4", {"start": v(-276.23, 5238.75) * mm, "end": v(-428.63, 5238.75) * mm});
            skLineSegment(sketch, "E7.24.6.4", {"start": v(-584.2, 4473.57) * mm, "end": v(-584.2, 5083.18) * mm});
            skLineSegment(sketch, "E7.27.6.4", {"start": v(-428.63, 4629.15) * mm, "end": v(-428.63, 5238.75) * mm});
            skLineSegment(sketch, "E7.30.6.4", {"start": v(25.4, 4318) * mm, "end": v(25.4, 4470.4) * mm});
            skLineSegment(sketch, "E7.33.6.4", {"start": v(-276.23, 4629.15) * mm, "end": v(-276.23, 5238.75) * mm});
            skLineSegment(sketch, "E7.36.6.4", {"start": v(-584.2, 4318) * mm, "end": v(-584.2, 4470.4) * mm});
            skLineSegment(sketch, "E7.39.6.4", {"start": v(-431.8, 5083.18) * mm, "end": v(-584.2, 5083.18) * mm});
            skLineSegment(sketch, "E7.42.6.4", {"start": v(180.97, 4473.57) * mm, "end": v(180.97, 4625.97) * mm});
            skLineSegment(sketch, "E7.45.6.4", {"start": v(-584.2, 4470.4) * mm, "end": v(25.4, 4470.4) * mm});
            skLineSegment(sketch, "E7.0.7.0", {"start": v(2178.05, 2178.05) * mm, "end": v(2787.65, 2178.05) * mm});
            skLineSegment(sketch, "E7.3.7.0", {"start": v(2330.45, 2333.62) * mm, "end": v(2178.05, 2333.62) * mm});
            skLineSegment(sketch, "E7.6.7.0", {"start": v(2333.63, 2333.62) * mm, "end": v(2333.63, 2486.02) * mm});
            skLineSegment(sketch, "E7.9.7.0", {"start": v(2486.03, 2489.2) * mm, "end": v(2333.63, 2489.2) * mm});
            skLineSegment(sketch, "E7.12.7.0", {"start": v(2333.63, 2333.62) * mm, "end": v(2943.23, 2333.62) * mm});
            skLineSegment(sketch, "E7.15.7.0", {"start": v(2330.45, 2333.62) * mm, "end": v(2330.45, 2943.22) * mm});
            skLineSegment(sketch, "E7.18.7.0", {"start": v(2333.63, 2486.02) * mm, "end": v(2943.23, 2486.02) * mm});
            skLineSegment(sketch, "E7.21.7.0", {"start": v(2486.03, 3098.8) * mm, "end": v(2333.63, 3098.8) * mm});
            skLineSegment(sketch, "E7.24.7.0", {"start": v(2178.05, 2333.62) * mm, "end": v(2178.05, 2943.22) * mm});
            skLineSegment(sketch, "E7.27.7.0", {"start": v(2333.63, 2489.2) * mm, "end": v(2333.63, 3098.8) * mm});
            skLineSegment(sketch, "E7.30.7.0", {"start": v(2787.65, 2178.05) * mm, "end": v(2787.65, 2330.45) * mm});
            skLineSegment(sketch, "E7.33.7.0", {"start": v(2486.03, 2489.2) * mm, "end": v(2486.03, 3098.8) * mm});
            skLineSegment(sketch, "E7.36.7.0", {"start": v(2178.05, 2178.05) * mm, "end": v(2178.05, 2330.45) * mm});
            skLineSegment(sketch, "E7.39.7.0", {"start": v(2330.45, 2943.22) * mm, "end": v(2178.05, 2943.22) * mm});
            skLineSegment(sketch, "E7.42.7.0", {"start": v(2943.23, 2333.62) * mm, "end": v(2943.23, 2486.02) * mm});
            skLineSegment(sketch, "E7.45.7.0", {"start": v(2178.05, 2330.45) * mm, "end": v(2787.65, 2330.45) * mm});
            skLineSegment(sketch, "E7.0.7.1", {"start": v(1565.28, 2790.82) * mm, "end": v(2174.88, 2790.82) * mm});
            skLineSegment(sketch, "E7.3.7.1", {"start": v(1717.68, 2946.4) * mm, "end": v(1565.28, 2946.4) * mm});
            skLineSegment(sketch, "E7.6.7.1", {"start": v(1720.85, 2946.4) * mm, "end": v(1720.85, 3098.8) * mm});
            skLineSegment(sketch, "E7.9.7.1", {"start": v(1873.25, 3101.97) * mm, "end": v(1720.85, 3101.97) * mm});
            skLineSegment(sketch, "E7.12.7.1", {"start": v(1720.85, 2946.4) * mm, "end": v(2330.45, 2946.4) * mm});
            skLineSegment(sketch, "E7.15.7.1", {"start": v(1717.68, 2946.4) * mm, "end": v(1717.68, 3556) * mm});
            skLineSegment(sketch, "E7.18.7.1", {"start": v(1720.85, 3098.8) * mm, "end": v(2330.45, 3098.8) * mm});
            skLineSegment(sketch, "E7.21.7.1", {"start": v(1873.25, 3711.57) * mm, "end": v(1720.85, 3711.57) * mm});
            skLineSegment(sketch, "E7.24.7.1", {"start": v(1565.28, 2946.4) * mm, "end": v(1565.28, 3556) * mm});
            skLineSegment(sketch, "E7.27.7.1", {"start": v(1720.85, 3101.97) * mm, "end": v(1720.85, 3711.57) * mm});
            skLineSegment(sketch, "E7.30.7.1", {"start": v(2174.88, 2790.82) * mm, "end": v(2174.88, 2943.22) * mm});
            skLineSegment(sketch, "E7.33.7.1", {"start": v(1873.25, 3101.97) * mm, "end": v(1873.25, 3711.57) * mm});
            skLineSegment(sketch, "E7.36.7.1", {"start": v(1565.28, 2790.82) * mm, "end": v(1565.28, 2943.22) * mm});
            skLineSegment(sketch, "E7.39.7.1", {"start": v(1717.68, 3556) * mm, "end": v(1565.28, 3556) * mm});
            skLineSegment(sketch, "E7.42.7.1", {"start": v(2330.45, 2946.4) * mm, "end": v(2330.45, 3098.8) * mm});
            skLineSegment(sketch, "E7.45.7.1", {"start": v(1565.28, 2943.22) * mm, "end": v(2174.88, 2943.22) * mm});
            skLineSegment(sketch, "E7.0.7.2", {"start": v(952.5, 3403.6) * mm, "end": v(1562.1, 3403.6) * mm});
            skLineSegment(sketch, "E7.3.7.2", {"start": v(1104.9, 3559.17) * mm, "end": v(952.5, 3559.17) * mm});
            skLineSegment(sketch, "E7.6.7.2", {"start": v(1108.07, 3559.17) * mm, "end": v(1108.07, 3711.57) * mm});
            skLineSegment(sketch, "E7.9.7.2", {"start": v(1260.47, 3714.75) * mm, "end": v(1108.07, 3714.75) * mm});
            skLineSegment(sketch, "E7.12.7.2", {"start": v(1108.07, 3559.17) * mm, "end": v(1717.67, 3559.17) * mm});
            skLineSegment(sketch, "E7.15.7.2", {"start": v(1104.9, 3559.17) * mm, "end": v(1104.9, 4168.77) * mm});
            skLineSegment(sketch, "E7.18.7.2", {"start": v(1108.07, 3711.57) * mm, "end": v(1717.67, 3711.57) * mm});
            skLineSegment(sketch, "E7.21.7.2", {"start": v(1260.47, 4324.35) * mm, "end": v(1108.07, 4324.35) * mm});
            skLineSegment(sketch, "E7.24.7.2", {"start": v(952.5, 3559.17) * mm, "end": v(952.5, 4168.77) * mm});
            skLineSegment(sketch, "E7.27.7.2", {"start": v(1108.07, 3714.75) * mm, "end": v(1108.07, 4324.35) * mm});
            skLineSegment(sketch, "E7.30.7.2", {"start": v(1562.1, 3403.6) * mm, "end": v(1562.1, 3556) * mm});
            skLineSegment(sketch, "E7.33.7.2", {"start": v(1260.47, 3714.75) * mm, "end": v(1260.47, 4324.35) * mm});
            skLineSegment(sketch, "E7.36.7.2", {"start": v(952.5, 3403.6) * mm, "end": v(952.5, 3556) * mm});
            skLineSegment(sketch, "E7.39.7.2", {"start": v(1104.9, 4168.77) * mm, "end": v(952.5, 4168.77) * mm});
            skLineSegment(sketch, "E7.42.7.2", {"start": v(1717.67, 3559.17) * mm, "end": v(1717.67, 3711.57) * mm});
            skLineSegment(sketch, "E7.45.7.2", {"start": v(952.5, 3556) * mm, "end": v(1562.1, 3556) * mm});
            skLineSegment(sketch, "E7.0.7.3", {"start": v(339.72, 4016.38) * mm, "end": v(949.32, 4016.38) * mm});
            skLineSegment(sketch, "E7.3.7.3", {"start": v(492.12, 4171.95) * mm, "end": v(339.72, 4171.95) * mm});
            skLineSegment(sketch, "E7.6.7.3", {"start": v(495.3, 4171.95) * mm, "end": v(495.3, 4324.35) * mm});
            skLineSegment(sketch, "E7.9.7.3", {"start": v(647.7, 4327.52) * mm, "end": v(495.3, 4327.52) * mm});
            skLineSegment(sketch, "E7.12.7.3", {"start": v(495.3, 4171.95) * mm, "end": v(1104.9, 4171.95) * mm});
            skLineSegment(sketch, "E7.15.7.3", {"start": v(492.12, 4171.95) * mm, "end": v(492.12, 4781.55) * mm});
            skLineSegment(sketch, "E7.18.7.3", {"start": v(495.3, 4324.35) * mm, "end": v(1104.9, 4324.35) * mm});
            skLineSegment(sketch, "E7.21.7.3", {"start": v(647.7, 4937.12) * mm, "end": v(495.3, 4937.12) * mm});
            skLineSegment(sketch, "E7.24.7.3", {"start": v(339.72, 4171.95) * mm, "end": v(339.72, 4781.55) * mm});
            skLineSegment(sketch, "E7.27.7.3", {"start": v(495.3, 4327.52) * mm, "end": v(495.3, 4937.12) * mm});
            skLineSegment(sketch, "E7.30.7.3", {"start": v(949.32, 4016.38) * mm, "end": v(949.32, 4168.78) * mm});
            skLineSegment(sketch, "E7.33.7.3", {"start": v(647.7, 4327.52) * mm, "end": v(647.7, 4937.12) * mm});
            skLineSegment(sketch, "E7.36.7.3", {"start": v(339.72, 4016.38) * mm, "end": v(339.72, 4168.78) * mm});
            skLineSegment(sketch, "E7.39.7.3", {"start": v(492.12, 4781.55) * mm, "end": v(339.72, 4781.55) * mm});
            skLineSegment(sketch, "E7.42.7.3", {"start": v(1104.9, 4171.95) * mm, "end": v(1104.9, 4324.35) * mm});
            skLineSegment(sketch, "E7.45.7.3", {"start": v(339.72, 4168.78) * mm, "end": v(949.32, 4168.78) * mm});
            skLineSegment(sketch, "E7.0.7.4", {"start": v(-273.05, 4629.15) * mm, "end": v(336.55, 4629.15) * mm});
            skLineSegment(sketch, "E7.3.7.4", {"start": v(-120.65, 4784.72) * mm, "end": v(-273.05, 4784.72) * mm});
            skLineSegment(sketch, "E7.6.7.4", {"start": v(-117.48, 4784.72) * mm, "end": v(-117.48, 4937.12) * mm});
            skLineSegment(sketch, "E7.9.7.4", {"start": v(34.92, 4940.3) * mm, "end": v(-117.48, 4940.3) * mm});
            skLineSegment(sketch, "E7.12.7.4", {"start": v(-117.48, 4784.72) * mm, "end": v(492.12, 4784.72) * mm});
            skLineSegment(sketch, "E7.15.7.4", {"start": v(-120.65, 4784.72) * mm, "end": v(-120.65, 5394.32) * mm});
            skLineSegment(sketch, "E7.18.7.4", {"start": v(-117.48, 4937.12) * mm, "end": v(492.12, 4937.12) * mm});
            skLineSegment(sketch, "E7.21.7.4", {"start": v(34.92, 5549.9) * mm, "end": v(-117.48, 5549.9) * mm});
            skLineSegment(sketch, "E7.24.7.4", {"start": v(-273.05, 4784.72) * mm, "end": v(-273.05, 5394.32) * mm});
            skLineSegment(sketch, "E7.27.7.4", {"start": v(-117.48, 4940.3) * mm, "end": v(-117.48, 5549.9) * mm});
            skLineSegment(sketch, "E7.30.7.4", {"start": v(336.55, 4629.15) * mm, "end": v(336.55, 4781.55) * mm});
            skLineSegment(sketch, "E7.33.7.4", {"start": v(34.92, 4940.3) * mm, "end": v(34.92, 5549.9) * mm});
            skLineSegment(sketch, "E7.36.7.4", {"start": v(-273.05, 4629.15) * mm, "end": v(-273.05, 4781.55) * mm});
            skLineSegment(sketch, "E7.39.7.4", {"start": v(-120.65, 5394.32) * mm, "end": v(-273.05, 5394.32) * mm});
            skLineSegment(sketch, "E7.42.7.4", {"start": v(492.12, 4784.72) * mm, "end": v(492.12, 4937.12) * mm});
            skLineSegment(sketch, "E7.45.7.4", {"start": v(-273.05, 4781.55) * mm, "end": v(336.55, 4781.55) * mm});
            skLineSegment(sketch, "E8.0.8.0", {"start": v(2489.2, 2489.2) * mm, "end": v(3098.8, 2489.2) * mm});
            skLineSegment(sketch, "E8.3.8.0", {"start": v(2641.6, 2644.77) * mm, "end": v(2489.2, 2644.77) * mm});
            skLineSegment(sketch, "E8.6.8.0", {"start": v(2644.78, 2644.77) * mm, "end": v(2644.78, 2797.17) * mm});
            skLineSegment(sketch, "E8.9.8.0", {"start": v(2797.18, 2800.35) * mm, "end": v(2644.78, 2800.35) * mm});
            skLineSegment(sketch, "E8.12.8.0", {"start": v(2644.78, 2644.77) * mm, "end": v(3254.38, 2644.77) * mm});
            skLineSegment(sketch, "E8.15.8.0", {"start": v(2641.6, 2644.77) * mm, "end": v(2641.6, 3254.37) * mm});
            skLineSegment(sketch, "E8.18.8.0", {"start": v(2644.78, 2797.17) * mm, "end": v(3254.38, 2797.17) * mm});
            skLineSegment(sketch, "E8.21.8.0", {"start": v(2797.18, 3409.95) * mm, "end": v(2644.78, 3409.95) * mm});
            skLineSegment(sketch, "E8.24.8.0", {"start": v(2489.2, 2644.77) * mm, "end": v(2489.2, 3254.37) * mm});
            skLineSegment(sketch, "E8.27.8.0", {"start": v(2644.78, 2800.35) * mm, "end": v(2644.78, 3409.95) * mm});
            skLineSegment(sketch, "E8.30.8.0", {"start": v(3098.8, 2489.2) * mm, "end": v(3098.8, 2641.6) * mm});
            skLineSegment(sketch, "E8.33.8.0", {"start": v(2797.18, 2800.35) * mm, "end": v(2797.18, 3409.95) * mm});
            skLineSegment(sketch, "E8.36.8.0", {"start": v(2489.2, 2489.2) * mm, "end": v(2489.2, 2641.6) * mm});
            skLineSegment(sketch, "E8.39.8.0", {"start": v(2641.6, 3254.37) * mm, "end": v(2489.2, 3254.37) * mm});
            skLineSegment(sketch, "E8.42.8.0", {"start": v(3254.38, 2644.77) * mm, "end": v(3254.38, 2797.17) * mm});
            skLineSegment(sketch, "E8.45.8.0", {"start": v(2489.2, 2641.6) * mm, "end": v(3098.8, 2641.6) * mm});
            skLineSegment(sketch, "E8.0.8.1", {"start": v(1876.43, 3101.97) * mm, "end": v(2486.03, 3101.97) * mm});
            skLineSegment(sketch, "E8.3.8.1", {"start": v(2028.83, 3257.55) * mm, "end": v(1876.43, 3257.55) * mm});
            skLineSegment(sketch, "E8.6.8.1", {"start": v(2032, 3257.55) * mm, "end": v(2032, 3409.95) * mm});
            skLineSegment(sketch, "E8.9.8.1", {"start": v(2184.4, 3413.12) * mm, "end": v(2032, 3413.12) * mm});
            skLineSegment(sketch, "E8.12.8.1", {"start": v(2032, 3257.55) * mm, "end": v(2641.6, 3257.55) * mm});
            skLineSegment(sketch, "E8.15.8.1", {"start": v(2028.83, 3257.55) * mm, "end": v(2028.83, 3867.15) * mm});
            skLineSegment(sketch, "E8.18.8.1", {"start": v(2032, 3409.95) * mm, "end": v(2641.6, 3409.95) * mm});
            skLineSegment(sketch, "E8.21.8.1", {"start": v(2184.4, 4022.72) * mm, "end": v(2032, 4022.72) * mm});
            skLineSegment(sketch, "E8.24.8.1", {"start": v(1876.43, 3257.55) * mm, "end": v(1876.43, 3867.15) * mm});
            skLineSegment(sketch, "E8.27.8.1", {"start": v(2032, 3413.12) * mm, "end": v(2032, 4022.72) * mm});
            skLineSegment(sketch, "E8.30.8.1", {"start": v(2486.03, 3101.97) * mm, "end": v(2486.03, 3254.37) * mm});
            skLineSegment(sketch, "E8.33.8.1", {"start": v(2184.4, 3413.12) * mm, "end": v(2184.4, 4022.72) * mm});
            skLineSegment(sketch, "E8.36.8.1", {"start": v(1876.43, 3101.97) * mm, "end": v(1876.43, 3254.37) * mm});
            skLineSegment(sketch, "E8.39.8.1", {"start": v(2028.83, 3867.15) * mm, "end": v(1876.43, 3867.15) * mm});
            skLineSegment(sketch, "E8.42.8.1", {"start": v(2641.6, 3257.55) * mm, "end": v(2641.6, 3409.95) * mm});
            skLineSegment(sketch, "E8.45.8.1", {"start": v(1876.43, 3254.37) * mm, "end": v(2486.03, 3254.37) * mm});
            skLineSegment(sketch, "E8.0.8.2", {"start": v(1263.65, 3714.75) * mm, "end": v(1873.25, 3714.75) * mm});
            skLineSegment(sketch, "E8.3.8.2", {"start": v(1416.05, 3870.32) * mm, "end": v(1263.65, 3870.32) * mm});
            skLineSegment(sketch, "E8.6.8.2", {"start": v(1419.22, 3870.32) * mm, "end": v(1419.22, 4022.72) * mm});
            skLineSegment(sketch, "E8.9.8.2", {"start": v(1571.62, 4025.9) * mm, "end": v(1419.22, 4025.9) * mm});
            skLineSegment(sketch, "E8.12.8.2", {"start": v(1419.22, 3870.32) * mm, "end": v(2028.82, 3870.32) * mm});
            skLineSegment(sketch, "E8.15.8.2", {"start": v(1416.05, 3870.32) * mm, "end": v(1416.05, 4479.92) * mm});
            skLineSegment(sketch, "E8.18.8.2", {"start": v(1419.22, 4022.72) * mm, "end": v(2028.82, 4022.72) * mm});
            skLineSegment(sketch, "E8.21.8.2", {"start": v(1571.62, 4635.5) * mm, "end": v(1419.22, 4635.5) * mm});
            skLineSegment(sketch, "E8.24.8.2", {"start": v(1263.65, 3870.32) * mm, "end": v(1263.65, 4479.92) * mm});
            skLineSegment(sketch, "E8.27.8.2", {"start": v(1419.22, 4025.9) * mm, "end": v(1419.22, 4635.5) * mm});
            skLineSegment(sketch, "E8.30.8.2", {"start": v(1873.25, 3714.75) * mm, "end": v(1873.25, 3867.15) * mm});
            skLineSegment(sketch, "E8.33.8.2", {"start": v(1571.62, 4025.9) * mm, "end": v(1571.62, 4635.5) * mm});
            skLineSegment(sketch, "E8.36.8.2", {"start": v(1263.65, 3714.75) * mm, "end": v(1263.65, 3867.15) * mm});
            skLineSegment(sketch, "E8.39.8.2", {"start": v(1416.05, 4479.92) * mm, "end": v(1263.65, 4479.92) * mm});
            skLineSegment(sketch, "E8.42.8.2", {"start": v(2028.82, 3870.32) * mm, "end": v(2028.82, 4022.72) * mm});
            skLineSegment(sketch, "E8.45.8.2", {"start": v(1263.65, 3867.15) * mm, "end": v(1873.25, 3867.15) * mm});
            skLineSegment(sketch, "E8.0.8.3", {"start": v(650.87, 4327.52) * mm, "end": v(1260.47, 4327.52) * mm});
            skLineSegment(sketch, "E8.3.8.3", {"start": v(803.27, 4483.1) * mm, "end": v(650.87, 4483.1) * mm});
            skLineSegment(sketch, "E8.6.8.3", {"start": v(806.45, 4483.1) * mm, "end": v(806.45, 4635.5) * mm});
            skLineSegment(sketch, "E8.9.8.3", {"start": v(958.85, 4638.67) * mm, "end": v(806.45, 4638.67) * mm});
            skLineSegment(sketch, "E8.12.8.3", {"start": v(806.45, 4483.1) * mm, "end": v(1416.05, 4483.1) * mm});
            skLineSegment(sketch, "E8.15.8.3", {"start": v(803.27, 4483.1) * mm, "end": v(803.27, 5092.7) * mm});
            skLineSegment(sketch, "E8.18.8.3", {"start": v(806.45, 4635.5) * mm, "end": v(1416.05, 4635.5) * mm});
            skLineSegment(sketch, "E8.21.8.3", {"start": v(958.85, 5248.27) * mm, "end": v(806.45, 5248.27) * mm});
            skLineSegment(sketch, "E8.24.8.3", {"start": v(650.87, 4483.1) * mm, "end": v(650.87, 5092.7) * mm});
            skLineSegment(sketch, "E8.27.8.3", {"start": v(806.45, 4638.67) * mm, "end": v(806.45, 5248.27) * mm});
            skLineSegment(sketch, "E8.30.8.3", {"start": v(1260.47, 4327.52) * mm, "end": v(1260.47, 4479.92) * mm});
            skLineSegment(sketch, "E8.33.8.3", {"start": v(958.85, 4638.67) * mm, "end": v(958.85, 5248.27) * mm});
            skLineSegment(sketch, "E8.36.8.3", {"start": v(650.87, 4327.52) * mm, "end": v(650.87, 4479.92) * mm});
            skLineSegment(sketch, "E8.39.8.3", {"start": v(803.27, 5092.7) * mm, "end": v(650.87, 5092.7) * mm});
            skLineSegment(sketch, "E8.42.8.3", {"start": v(1416.05, 4483.1) * mm, "end": v(1416.05, 4635.5) * mm});
            skLineSegment(sketch, "E8.45.8.3", {"start": v(650.87, 4479.92) * mm, "end": v(1260.47, 4479.92) * mm});
            skLineSegment(sketch, "E8.0.8.4", {"start": v(38.1, 4940.3) * mm, "end": v(647.7, 4940.3) * mm});
            skLineSegment(sketch, "E8.3.8.4", {"start": v(190.5, 5095.87) * mm, "end": v(38.1, 5095.87) * mm});
            skLineSegment(sketch, "E8.6.8.4", {"start": v(193.67, 5095.87) * mm, "end": v(193.67, 5248.27) * mm});
            skLineSegment(sketch, "E8.9.8.4", {"start": v(346.07, 5251.45) * mm, "end": v(193.67, 5251.45) * mm});
            skLineSegment(sketch, "E8.12.8.4", {"start": v(193.67, 5095.87) * mm, "end": v(803.27, 5095.87) * mm});
            skLineSegment(sketch, "E8.15.8.4", {"start": v(190.5, 5095.87) * mm, "end": v(190.5, 5705.47) * mm});
            skLineSegment(sketch, "E8.18.8.4", {"start": v(193.67, 5248.27) * mm, "end": v(803.27, 5248.27) * mm});
            skLineSegment(sketch, "E8.21.8.4", {"start": v(346.07, 5861.05) * mm, "end": v(193.67, 5861.05) * mm});
            skLineSegment(sketch, "E8.24.8.4", {"start": v(38.1, 5095.87) * mm, "end": v(38.1, 5705.47) * mm});
            skLineSegment(sketch, "E8.27.8.4", {"start": v(193.67, 5251.45) * mm, "end": v(193.67, 5861.05) * mm});
            skLineSegment(sketch, "E8.30.8.4", {"start": v(647.7, 4940.3) * mm, "end": v(647.7, 5092.7) * mm});
            skLineSegment(sketch, "E8.33.8.4", {"start": v(346.07, 5251.45) * mm, "end": v(346.07, 5861.05) * mm});
            skLineSegment(sketch, "E8.36.8.4", {"start": v(38.1, 4940.3) * mm, "end": v(38.1, 5092.7) * mm});
            skLineSegment(sketch, "E8.39.8.4", {"start": v(190.5, 5705.47) * mm, "end": v(38.1, 5705.47) * mm});
            skLineSegment(sketch, "E8.42.8.4", {"start": v(803.27, 5095.87) * mm, "end": v(803.27, 5248.27) * mm});
            skLineSegment(sketch, "E8.45.8.4", {"start": v(38.1, 5092.7) * mm, "end": v(647.7, 5092.7) * mm});
            skSolve(sketch);
        }
        {
            var Q0;
            Q0 = qSketchRegion(id + "F0", true);
            extrude(context, id + "F1", {"entities" : qUnion([Q0]), "depth" : 6.35 * mm, "offsetDistance" : 25.4 * mm});
        }
        {
            var Q0;
            Q0=qCreatedBy(makeId("Top.planeOp"),FACE);
            var sketch = newSketch(context, id + "F2", { "sketchPlane" : qUnion([Q0])});
            skLineSegment(sketch, "E9", {"start": v(-267.36, 4162.97) * mm, "end": v(-1367.44, 3062.89) * mm});
            skLineSegment(sketch, "E10", {"start": v(-1367.44, 3062.89) * mm, "end": v(-78.77, 1774.22) * mm});
            skLineSegment(sketch, "E11", {"start": v(-78.77, 1774.22) * mm, "end": v(1021.3, 2874.3) * mm});
            skLineSegment(sketch, "E12", {"start": v(1021.3, 2874.3) * mm, "end": v(-267.36, 4162.97) * mm});
            skLineSegment(sketch, "E13.bottom", {"start": v(-4816.06, 8587.4) * mm, "end": v(6787.9, 8587.4) * mm});
            skLineSegment(sketch, "E13.top", {"start": v(-4816.06, -1489.72) * mm, "end": v(6787.9, -1489.72) * mm});
            skLineSegment(sketch, "E13.left", {"start": v(-4816.06, 8587.4) * mm, "end": v(-4816.06, -1489.72) * mm});
            skLineSegment(sketch, "E13.right", {"start": v(6787.9, 8587.4) * mm, "end": v(6787.9, -1489.72) * mm});
            skLineSegment(sketch, "E14", {"start": v(327.03, 3546.47) * mm, "end": v(171.45, 3390.9) * mm, "construction": true});
            skLineSegment(sketch, "E15", {"start": v(327.03, 3390.9) * mm, "end": v(171.45, 3235.32) * mm, "construction": true});
            skLineSegment(sketch, "E16", {"start": v(205.93, 3425.38) * mm, "end": v(283.71, 3347.59) * mm, "construction": true});
            skLineSegment(sketch, "E17", {"start": v(376.98, 3518.64) * mm, "end": v(244.82, 3386.48) * mm, "construction": true});
            skSolve(sketch);
        }
        {
            var Q0;
            Q0 = qSketchRegion(id + "F2", true);
            extrude(context, id + "F3", {"entities" : qUnion([Q0]), "operationType" : NewBodyOperationType.REMOVE, "endBound" : BoundingType.THROUGH_ALL, "depth" : 25.4 * mm, "offsetDistance" : 25.4 * mm});
        }
        {
            var Q0;
            Q0=makeQuery(id+"F1.opExtrude","SWEPT_BODY",BODY,{"disambiguationData":[OSD([sQuery(id+"F0.wireOp",EDGE,"E4.1.1.3"),sQuery(id+"F0.wireOp",EDGE,"E4.1.1.7"),sQuery(id+"F0.wireOp",EDGE,"E4.1.1.9"),sQuery(id+"F0.wireOp",EDGE,"E4.1.1.11")])]});
            var Q1;
            Q1=makeQuery(id+"F1.opExtrude","SWEPT_BODY",BODY,{"disambiguationData":[OSD([sQuery(id+"F0.wireOp",EDGE,"E4.2.1.1"),sQuery(id+"F0.wireOp",EDGE,"E4.2.1.5"),sQuery(id+"F0.wireOp",EDGE,"E4.2.1.8"),sQuery(id+"F0.wireOp",EDGE,"E4.2.1.13")])]});
            var Q2;
            Q2=makeQuery(id+"F1.opExtrude","SWEPT_BODY",BODY,{"disambiguationData":[OSD([sQuery(id+"F0.wireOp",EDGE,"E4.2.1.3"),sQuery(id+"F0.wireOp",EDGE,"E4.2.1.7"),sQuery(id+"F0.wireOp",EDGE,"E4.2.1.9"),sQuery(id+"F0.wireOp",EDGE,"E4.2.1.11")])]});
            var Q3;
            Q3=makeQuery(id+"F1.opExtrude","SWEPT_BODY",BODY,{"disambiguationData":[OSD([sQuery(id+"F0.wireOp",EDGE,"E5.3.3.1"),sQuery(id+"F0.wireOp",EDGE,"E5.15.3.1"),sQuery(id+"F0.wireOp",EDGE,"E5.24.3.1"),sQuery(id+"F0.wireOp",EDGE,"E5.39.3.1")])]});
            var Q4;
            Q4=makeQuery(id+"F1.opExtrude","SWEPT_BODY",BODY,{"disambiguationData":[OSD([sQuery(id+"F0.wireOp",EDGE,"E5.9.3.1"),sQuery(id+"F0.wireOp",EDGE,"E5.21.3.1"),sQuery(id+"F0.wireOp",EDGE,"E5.27.3.1"),sQuery(id+"F0.wireOp",EDGE,"E5.33.3.1")])]});
            var Q5;
            Q5=makeQuery(id+"F1.opExtrude","SWEPT_BODY",BODY,{"disambiguationData":[OSD([sQuery(id+"F0.wireOp",EDGE,"E5.3.4.1"),sQuery(id+"F0.wireOp",EDGE,"E5.15.4.1"),sQuery(id+"F0.wireOp",EDGE,"E5.24.4.1"),sQuery(id+"F0.wireOp",EDGE,"E5.39.4.1")])]});
            var Q6;
            Q6=makeQuery(id+"F1.opExtrude","SWEPT_BODY",BODY,{"disambiguationData":[OSD([sQuery(id+"F0.wireOp",EDGE,"E5.9.4.1"),sQuery(id+"F0.wireOp",EDGE,"E5.21.4.1"),sQuery(id+"F0.wireOp",EDGE,"E5.27.4.1"),sQuery(id+"F0.wireOp",EDGE,"E5.33.4.1")])]});
            var Q7;
            Q7=makeQuery(id+"F1.opExtrude","SWEPT_BODY",BODY,{"disambiguationData":[OSD([sQuery(id+"F0.wireOp",EDGE,"E5.3.5.1"),sQuery(id+"F0.wireOp",EDGE,"E5.15.5.1"),sQuery(id+"F0.wireOp",EDGE,"E5.24.5.1"),sQuery(id+"F0.wireOp",EDGE,"E5.39.5.1")])]});
            var Q8;
            Q8=makeQuery(id+"F1.opExtrude","SWEPT_BODY",BODY,{"disambiguationData":[OSD([sQuery(id+"F0.wireOp",EDGE,"E6.9.1.2"),sQuery(id+"F0.wireOp",EDGE,"E6.21.1.2"),sQuery(id+"F0.wireOp",EDGE,"E6.27.1.2"),sQuery(id+"F0.wireOp",EDGE,"E6.33.1.2")])]});
            var Q9;
            Q9=makeQuery(id+"F1.opExtrude","SWEPT_BODY",BODY,{"disambiguationData":[OSD([sQuery(id+"F0.wireOp",EDGE,"E6.9.1.3"),sQuery(id+"F0.wireOp",EDGE,"E6.21.1.3"),sQuery(id+"F0.wireOp",EDGE,"E6.27.1.3"),sQuery(id+"F0.wireOp",EDGE,"E6.33.1.3")])]});
            var Q10;
            Q10=makeQuery(id+"F1.opExtrude","SWEPT_BODY",BODY,{"disambiguationData":[OSD([sQuery(id+"F0.wireOp",EDGE,"E6.0.2.2"),sQuery(id+"F0.wireOp",EDGE,"E6.30.2.2"),sQuery(id+"F0.wireOp",EDGE,"E6.36.2.2"),sQuery(id+"F0.wireOp",EDGE,"E6.45.2.2")])]});
            var Q11;
            Q11=makeQuery(id+"F1.opExtrude","SWEPT_BODY",BODY,{"disambiguationData":[OSD([sQuery(id+"F0.wireOp",EDGE,"E6.3.2.2"),sQuery(id+"F0.wireOp",EDGE,"E6.15.2.2"),sQuery(id+"F0.wireOp",EDGE,"E6.24.2.2"),sQuery(id+"F0.wireOp",EDGE,"E6.39.2.2")])]});
            var Q12;
            Q12=makeQuery(id+"F1.opExtrude","SWEPT_BODY",BODY,{"disambiguationData":[OSD([sQuery(id+"F0.wireOp",EDGE,"E6.6.2.2"),sQuery(id+"F0.wireOp",EDGE,"E6.12.2.2"),sQuery(id+"F0.wireOp",EDGE,"E6.18.2.2"),sQuery(id+"F0.wireOp",EDGE,"E6.42.2.2")])]});
            var Q13;
            Q13=makeQuery(id+"F1.opExtrude","SWEPT_BODY",BODY,{"disambiguationData":[OSD([sQuery(id+"F0.wireOp",EDGE,"E6.9.2.2"),sQuery(id+"F0.wireOp",EDGE,"E6.21.2.2"),sQuery(id+"F0.wireOp",EDGE,"E6.27.2.2"),sQuery(id+"F0.wireOp",EDGE,"E6.33.2.2")])]});
            var Q14;
            Q14=makeQuery(id+"F1.opExtrude","SWEPT_BODY",BODY,{"disambiguationData":[OSD([sQuery(id+"F0.wireOp",EDGE,"E6.0.2.3"),sQuery(id+"F0.wireOp",EDGE,"E6.30.2.3"),sQuery(id+"F0.wireOp",EDGE,"E6.36.2.3"),sQuery(id+"F0.wireOp",EDGE,"E6.45.2.3")])]});
            var Q15;
            Q15=makeQuery(id+"F1.opExtrude","SWEPT_BODY",BODY,{"disambiguationData":[OSD([sQuery(id+"F0.wireOp",EDGE,"E6.3.2.3"),sQuery(id+"F0.wireOp",EDGE,"E6.15.2.3"),sQuery(id+"F0.wireOp",EDGE,"E6.24.2.3"),sQuery(id+"F0.wireOp",EDGE,"E6.39.2.3")])]});
            var Q16;
            Q16=makeQuery(id+"F1.opExtrude","SWEPT_BODY",BODY,{"disambiguationData":[OSD([sQuery(id+"F0.wireOp",EDGE,"E6.6.2.3"),sQuery(id+"F0.wireOp",EDGE,"E6.12.2.3"),sQuery(id+"F0.wireOp",EDGE,"E6.18.2.3"),sQuery(id+"F0.wireOp",EDGE,"E6.42.2.3")])]});
            var Q17;
            Q17=makeQuery(id+"F1.opExtrude","SWEPT_BODY",BODY,{"disambiguationData":[OSD([sQuery(id+"F0.wireOp",EDGE,"E6.9.2.3"),sQuery(id+"F0.wireOp",EDGE,"E6.21.2.3"),sQuery(id+"F0.wireOp",EDGE,"E6.27.2.3"),sQuery(id+"F0.wireOp",EDGE,"E6.33.2.3")])]});
            var Q18;
            Q18=makeQuery(id+"F1.opExtrude","SWEPT_BODY",BODY,{"disambiguationData":[OSD([sQuery(id+"F0.wireOp",EDGE,"E6.0.2.4"),sQuery(id+"F0.wireOp",EDGE,"E6.30.2.4"),sQuery(id+"F0.wireOp",EDGE,"E6.36.2.4"),sQuery(id+"F0.wireOp",EDGE,"E6.45.2.4")])]});
            var Q19;
            Q19=makeQuery(id+"F1.opExtrude","SWEPT_BODY",BODY,{"disambiguationData":[OSD([sQuery(id+"F0.wireOp",EDGE,"E6.6.2.4"),sQuery(id+"F0.wireOp",EDGE,"E6.12.2.4"),sQuery(id+"F0.wireOp",EDGE,"E6.18.2.4"),sQuery(id+"F0.wireOp",EDGE,"E6.42.2.4")])]});
            var Q20;
            Q20=makeQuery(id+"F1.opExtrude","SWEPT_BODY",BODY,{"disambiguationData":[OSD([sQuery(id+"F0.wireOp",EDGE,"E6.0.3.2"),sQuery(id+"F0.wireOp",EDGE,"E6.30.3.2"),sQuery(id+"F0.wireOp",EDGE,"E6.36.3.2"),sQuery(id+"F0.wireOp",EDGE,"E6.45.3.2")])]});
            var Q21;
            Q21=makeQuery(id+"F1.opExtrude","SWEPT_BODY",BODY,{"disambiguationData":[OSD([sQuery(id+"F0.wireOp",EDGE,"E6.3.3.2"),sQuery(id+"F0.wireOp",EDGE,"E6.15.3.2"),sQuery(id+"F0.wireOp",EDGE,"E6.24.3.2"),sQuery(id+"F0.wireOp",EDGE,"E6.39.3.2")])]});
            var Q22;
            Q22=makeQuery(id+"F1.opExtrude","SWEPT_BODY",BODY,{"disambiguationData":[OSD([sQuery(id+"F0.wireOp",EDGE,"E6.6.3.2"),sQuery(id+"F0.wireOp",EDGE,"E6.12.3.2"),sQuery(id+"F0.wireOp",EDGE,"E6.18.3.2"),sQuery(id+"F0.wireOp",EDGE,"E6.42.3.2")])]});
            var Q23;
            Q23=makeQuery(id+"F1.opExtrude","SWEPT_BODY",BODY,{"disambiguationData":[OSD([sQuery(id+"F0.wireOp",EDGE,"E6.9.3.2"),sQuery(id+"F0.wireOp",EDGE,"E6.21.3.2"),sQuery(id+"F0.wireOp",EDGE,"E6.27.3.2"),sQuery(id+"F0.wireOp",EDGE,"E6.33.3.2")])]});
            var Q24;
            Q24=makeQuery(id+"F1.opExtrude","SWEPT_BODY",BODY,{"disambiguationData":[OSD([sQuery(id+"F0.wireOp",EDGE,"E6.0.3.3"),sQuery(id+"F0.wireOp",EDGE,"E6.30.3.3"),sQuery(id+"F0.wireOp",EDGE,"E6.36.3.3"),sQuery(id+"F0.wireOp",EDGE,"E6.45.3.3")])]});
            var Q25;
            Q25=makeQuery(id+"F1.opExtrude","SWEPT_BODY",BODY,{"disambiguationData":[OSD([sQuery(id+"F0.wireOp",EDGE,"E6.3.3.3"),sQuery(id+"F0.wireOp",EDGE,"E6.15.3.3"),sQuery(id+"F0.wireOp",EDGE,"E6.24.3.3"),sQuery(id+"F0.wireOp",EDGE,"E6.39.3.3")])]});
            var Q26;
            Q26=makeQuery(id+"F1.opExtrude","SWEPT_BODY",BODY,{"disambiguationData":[OSD([sQuery(id+"F0.wireOp",EDGE,"E6.6.3.3"),sQuery(id+"F0.wireOp",EDGE,"E6.12.3.3"),sQuery(id+"F0.wireOp",EDGE,"E6.18.3.3"),sQuery(id+"F0.wireOp",EDGE,"E6.42.3.3")])]});
            var Q27;
            Q27=makeQuery(id+"F1.opExtrude","SWEPT_BODY",BODY,{"disambiguationData":[OSD([sQuery(id+"F0.wireOp",EDGE,"E6.9.3.3"),sQuery(id+"F0.wireOp",EDGE,"E6.21.3.3"),sQuery(id+"F0.wireOp",EDGE,"E6.27.3.3"),sQuery(id+"F0.wireOp",EDGE,"E6.33.3.3")])]});
            var Q28;
            Q28=makeQuery(id+"F1.opExtrude","SWEPT_BODY",BODY,{"disambiguationData":[OSD([sQuery(id+"F0.wireOp",EDGE,"E6.0.3.4"),sQuery(id+"F0.wireOp",EDGE,"E6.30.3.4"),sQuery(id+"F0.wireOp",EDGE,"E6.36.3.4"),sQuery(id+"F0.wireOp",EDGE,"E6.45.3.4")])]});
            var Q29;
            Q29=makeQuery(id+"F1.opExtrude","SWEPT_BODY",BODY,{"disambiguationData":[OSD([sQuery(id+"F0.wireOp",EDGE,"E6.6.3.4"),sQuery(id+"F0.wireOp",EDGE,"E6.12.3.4"),sQuery(id+"F0.wireOp",EDGE,"E6.18.3.4"),sQuery(id+"F0.wireOp",EDGE,"E6.42.3.4")])]});
            var Q30;
            Q30=makeQuery(id+"F1.opExtrude","SWEPT_BODY",BODY,{"disambiguationData":[OSD([sQuery(id+"F0.wireOp",EDGE,"E6.0.4.2"),sQuery(id+"F0.wireOp",EDGE,"E6.30.4.2"),sQuery(id+"F0.wireOp",EDGE,"E6.36.4.2"),sQuery(id+"F0.wireOp",EDGE,"E6.45.4.2")])]});
            var Q31;
            Q31=makeQuery(id+"F1.opExtrude","SWEPT_BODY",BODY,{"disambiguationData":[OSD([sQuery(id+"F0.wireOp",EDGE,"E6.3.4.2"),sQuery(id+"F0.wireOp",EDGE,"E6.15.4.2"),sQuery(id+"F0.wireOp",EDGE,"E6.24.4.2"),sQuery(id+"F0.wireOp",EDGE,"E6.39.4.2")])]});
            var Q32;
            Q32=makeQuery(id+"F1.opExtrude","SWEPT_BODY",BODY,{"disambiguationData":[OSD([sQuery(id+"F0.wireOp",EDGE,"E6.6.4.2"),sQuery(id+"F0.wireOp",EDGE,"E6.12.4.2"),sQuery(id+"F0.wireOp",EDGE,"E6.18.4.2"),sQuery(id+"F0.wireOp",EDGE,"E6.42.4.2")])]});
            var Q33;
            Q33=makeQuery(id+"F1.opExtrude","SWEPT_BODY",BODY,{"disambiguationData":[OSD([sQuery(id+"F0.wireOp",EDGE,"E6.9.4.2"),sQuery(id+"F0.wireOp",EDGE,"E6.21.4.2"),sQuery(id+"F0.wireOp",EDGE,"E6.27.4.2"),sQuery(id+"F0.wireOp",EDGE,"E6.33.4.2")])]});
            var Q34;
            Q34=makeQuery(id+"F1.opExtrude","SWEPT_BODY",BODY,{"disambiguationData":[OSD([sQuery(id+"F0.wireOp",EDGE,"E6.0.4.3"),sQuery(id+"F0.wireOp",EDGE,"E6.30.4.3"),sQuery(id+"F0.wireOp",EDGE,"E6.36.4.3"),sQuery(id+"F0.wireOp",EDGE,"E6.45.4.3")])]});
            var Q35;
            Q35=makeQuery(id+"F1.opExtrude","SWEPT_BODY",BODY,{"disambiguationData":[OSD([sQuery(id+"F0.wireOp",EDGE,"E6.3.4.3"),sQuery(id+"F0.wireOp",EDGE,"E6.15.4.3"),sQuery(id+"F0.wireOp",EDGE,"E6.24.4.3"),sQuery(id+"F0.wireOp",EDGE,"E6.39.4.3")])]});
            var Q36;
            Q36=makeQuery(id+"F1.opExtrude","SWEPT_BODY",BODY,{"disambiguationData":[OSD([sQuery(id+"F0.wireOp",EDGE,"E6.6.4.3"),sQuery(id+"F0.wireOp",EDGE,"E6.12.4.3"),sQuery(id+"F0.wireOp",EDGE,"E6.18.4.3"),sQuery(id+"F0.wireOp",EDGE,"E6.42.4.3")])]});
            var Q37;
            Q37=makeQuery(id+"F1.opExtrude","SWEPT_BODY",BODY,{"disambiguationData":[OSD([sQuery(id+"F0.wireOp",EDGE,"E6.9.4.3"),sQuery(id+"F0.wireOp",EDGE,"E6.21.4.3"),sQuery(id+"F0.wireOp",EDGE,"E6.27.4.3"),sQuery(id+"F0.wireOp",EDGE,"E6.33.4.3")])]});
            var Q38;
            Q38=makeQuery(id+"F1.opExtrude","SWEPT_BODY",BODY,{"disambiguationData":[OSD([sQuery(id+"F0.wireOp",EDGE,"E6.0.4.4"),sQuery(id+"F0.wireOp",EDGE,"E6.30.4.4"),sQuery(id+"F0.wireOp",EDGE,"E6.36.4.4"),sQuery(id+"F0.wireOp",EDGE,"E6.45.4.4")])]});
            var Q39;
            Q39=makeQuery(id+"F1.opExtrude","SWEPT_BODY",BODY,{"disambiguationData":[OSD([sQuery(id+"F0.wireOp",EDGE,"E6.6.4.4"),sQuery(id+"F0.wireOp",EDGE,"E6.12.4.4"),sQuery(id+"F0.wireOp",EDGE,"E6.18.4.4"),sQuery(id+"F0.wireOp",EDGE,"E6.42.4.4")])]});
            var Q40;
            Q40=makeQuery(id+"F1.opExtrude","SWEPT_BODY",BODY,{"disambiguationData":[OSD([sQuery(id+"F0.wireOp",EDGE,"E6.0.5.2"),sQuery(id+"F0.wireOp",EDGE,"E6.30.5.2"),sQuery(id+"F0.wireOp",EDGE,"E6.36.5.2"),sQuery(id+"F0.wireOp",EDGE,"E6.45.5.2")])]});
            var Q41;
            Q41=makeQuery(id+"F1.opExtrude","SWEPT_BODY",BODY,{"disambiguationData":[OSD([sQuery(id+"F0.wireOp",EDGE,"E6.3.5.2"),sQuery(id+"F0.wireOp",EDGE,"E6.15.5.2"),sQuery(id+"F0.wireOp",EDGE,"E6.24.5.2"),sQuery(id+"F0.wireOp",EDGE,"E6.39.5.2")])]});
            var Q42;
            Q42=makeQuery(id+"F1.opExtrude","SWEPT_BODY",BODY,{"disambiguationData":[OSD([sQuery(id+"F0.wireOp",EDGE,"E6.6.5.2"),sQuery(id+"F0.wireOp",EDGE,"E6.12.5.2"),sQuery(id+"F0.wireOp",EDGE,"E6.18.5.2"),sQuery(id+"F0.wireOp",EDGE,"E6.42.5.2")])]});
            var Q43;
            Q43=makeQuery(id+"F1.opExtrude","SWEPT_BODY",BODY,{"disambiguationData":[OSD([sQuery(id+"F0.wireOp",EDGE,"E6.9.5.2"),sQuery(id+"F0.wireOp",EDGE,"E6.21.5.2"),sQuery(id+"F0.wireOp",EDGE,"E6.27.5.2"),sQuery(id+"F0.wireOp",EDGE,"E6.33.5.2")])]});
            var Q44;
            Q44=makeQuery(id+"F1.opExtrude","SWEPT_BODY",BODY,{"disambiguationData":[OSD([sQuery(id+"F0.wireOp",EDGE,"E6.0.5.3"),sQuery(id+"F0.wireOp",EDGE,"E6.30.5.3"),sQuery(id+"F0.wireOp",EDGE,"E6.36.5.3"),sQuery(id+"F0.wireOp",EDGE,"E6.45.5.3")])]});
            var Q45;
            Q45=makeQuery(id+"F1.opExtrude","SWEPT_BODY",BODY,{"disambiguationData":[OSD([sQuery(id+"F0.wireOp",EDGE,"E6.3.5.3"),sQuery(id+"F0.wireOp",EDGE,"E6.15.5.3"),sQuery(id+"F0.wireOp",EDGE,"E6.24.5.3"),sQuery(id+"F0.wireOp",EDGE,"E6.39.5.3")])]});
            var Q46;
            Q46=makeQuery(id+"F1.opExtrude","SWEPT_BODY",BODY,{"disambiguationData":[OSD([sQuery(id+"F0.wireOp",EDGE,"E6.6.5.3"),sQuery(id+"F0.wireOp",EDGE,"E6.12.5.3"),sQuery(id+"F0.wireOp",EDGE,"E6.18.5.3"),sQuery(id+"F0.wireOp",EDGE,"E6.42.5.3")])]});
            var Q47;
            Q47=makeQuery(id+"F1.opExtrude","SWEPT_BODY",BODY,{"disambiguationData":[OSD([sQuery(id+"F0.wireOp",EDGE,"E6.9.5.3"),sQuery(id+"F0.wireOp",EDGE,"E6.21.5.3"),sQuery(id+"F0.wireOp",EDGE,"E6.27.5.3"),sQuery(id+"F0.wireOp",EDGE,"E6.33.5.3")])]});
            var Q48;
            Q48=makeQuery(id+"F1.opExtrude","SWEPT_BODY",BODY,{"disambiguationData":[OSD([sQuery(id+"F0.wireOp",EDGE,"E6.0.5.4"),sQuery(id+"F0.wireOp",EDGE,"E6.30.5.4"),sQuery(id+"F0.wireOp",EDGE,"E6.36.5.4"),sQuery(id+"F0.wireOp",EDGE,"E6.45.5.4")])]});
            var Q49;
            Q49=makeQuery(id+"F1.opExtrude","SWEPT_BODY",BODY,{"disambiguationData":[OSD([sQuery(id+"F0.wireOp",EDGE,"E6.6.5.4"),sQuery(id+"F0.wireOp",EDGE,"E6.12.5.4"),sQuery(id+"F0.wireOp",EDGE,"E6.18.5.4"),sQuery(id+"F0.wireOp",EDGE,"E6.42.5.4")])]});
            var Q50;
            Q50=makeQuery(id+"F1.opExtrude","SWEPT_BODY",BODY,{"disambiguationData":[OSD([sQuery(id+"F0.wireOp",EDGE,"E7.0.6.2"),sQuery(id+"F0.wireOp",EDGE,"E7.30.6.2"),sQuery(id+"F0.wireOp",EDGE,"E7.36.6.2"),sQuery(id+"F0.wireOp",EDGE,"E7.45.6.2")])]});
            var Q51;
            Q51=makeQuery(id+"F1.opExtrude","SWEPT_BODY",BODY,{"disambiguationData":[OSD([sQuery(id+"F0.wireOp",EDGE,"E7.0.6.3"),sQuery(id+"F0.wireOp",EDGE,"E7.30.6.3"),sQuery(id+"F0.wireOp",EDGE,"E7.36.6.3"),sQuery(id+"F0.wireOp",EDGE,"E7.45.6.3")])]});
            var Q52;
            Q52=makeQuery(id+"F1.opExtrude","SWEPT_BODY",BODY,{"disambiguationData":[OSD([sQuery(id+"F0.wireOp",EDGE,"E7.3.6.2"),sQuery(id+"F0.wireOp",EDGE,"E7.15.6.2"),sQuery(id+"F0.wireOp",EDGE,"E7.24.6.2"),sQuery(id+"F0.wireOp",EDGE,"E7.39.6.2")])]});
            var Q53;
            Q53=makeQuery(id+"F1.opExtrude","SWEPT_BODY",BODY,{"disambiguationData":[OSD([sQuery(id+"F0.wireOp",EDGE,"E7.3.6.3"),sQuery(id+"F0.wireOp",EDGE,"E7.15.6.3"),sQuery(id+"F0.wireOp",EDGE,"E7.24.6.3"),sQuery(id+"F0.wireOp",EDGE,"E7.39.6.3")])]});
            var Q54;
            Q54=makeQuery(id+"F3.boolean.opBoolean","COPY",EDGE,{"derivedFrom":makeQuery(id+"F3.opExtrude","SWEPT_EDGE",EDGE,{"disambiguationData":[OSD([sQuery(id+"F2.wireOp",EDGE,"E9"),sQuery(id+"F2.wireOp",EDGE,"E10")])]})});
            transform(context, id + "F4", {"entities" : qUnion([Q0, Q1, Q2, Q3, Q4, Q5, Q6, Q7, Q8, Q9, Q10, Q11, Q12, Q13, Q14, Q15, Q16, Q17, Q18, Q19, Q20, Q21, Q22, Q23, Q24, Q25, Q26, Q27, Q28, Q29, Q30, Q31, Q32, Q33, Q34, Q35, Q36, Q37, Q38, Q39, Q40, Q41, Q42, Q43, Q44, Q45, Q46, Q47, Q48, Q49, Q50, Q51, Q52, Q53]), "transformType" : TransformType.ROTATION, "transformAxis" : qUnion([Q54]), "angle" : 45 * degree, "oppositeDirection" : true, "makeCopy" : false});
        }
    });
